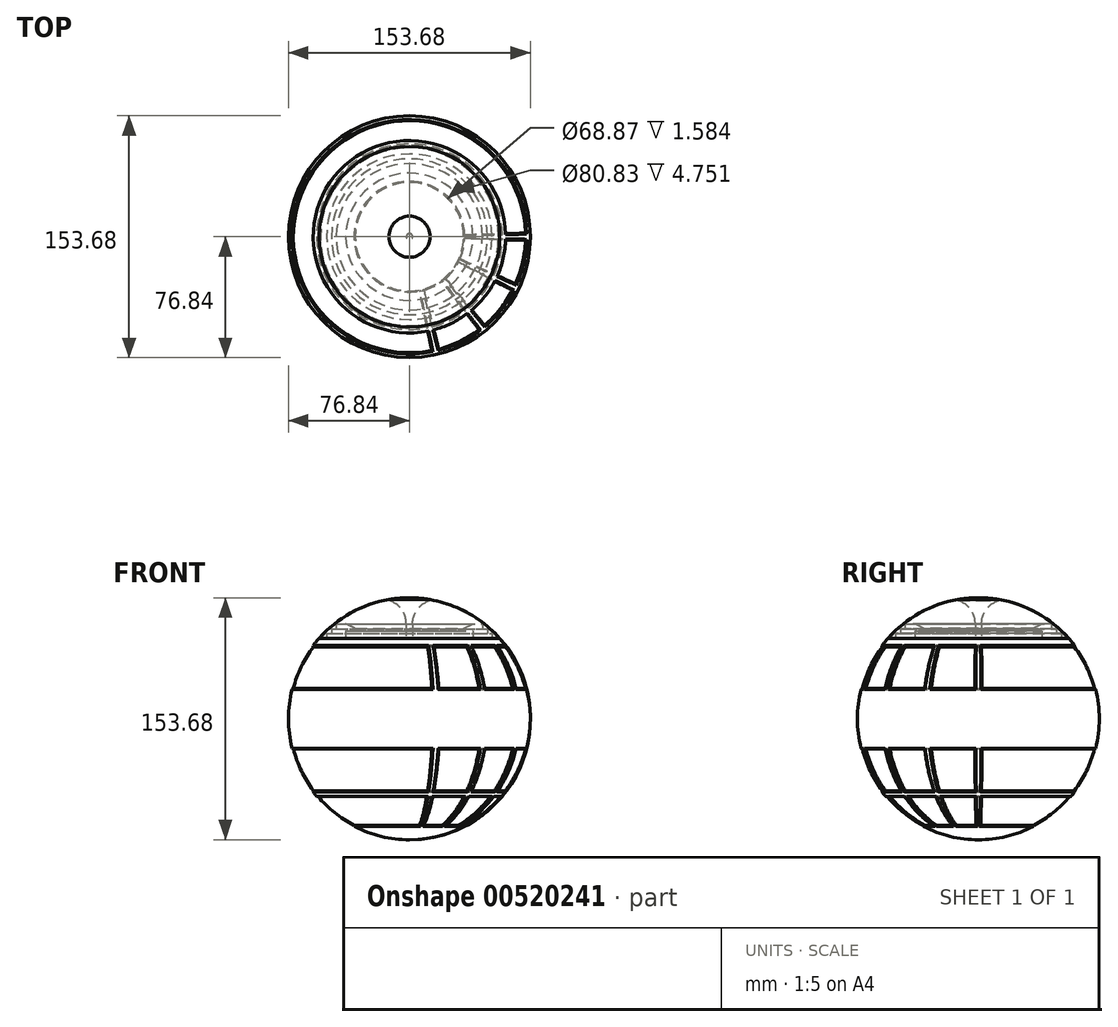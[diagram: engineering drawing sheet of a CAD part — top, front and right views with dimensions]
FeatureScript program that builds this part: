
annotation { "Feature Type Name" : "Feature", "Feature Type Description" : "" }
export const myFeature = defineFeature(function(context is Context, id is Id, definition is map)
    precondition{}
    {
        {
            var Q0;
            Q0=qCreatedBy(makeId("Front.planeOp"),FACE);
            var sketch = newSketch(context, id + "F0", { "sketchPlane" : qUnion([Q0])});
            skCircle(sketch, "E0", {"center": v(0, 0) * mm, "radius": 76.2 * mm});
            skLineSegment(sketch, "E1", {"start": v(0, 0) * mm, "end": v(74.29, 16.95) * mm, "construction": true});
            skLineSegment(sketch, "E2", {"start": v(0, 0) * mm, "end": v(74.29, -16.96) * mm, "construction": true});
            skLineSegment(sketch, "E3", {"start": v(0, 0) * mm, "end": v(59.58, -47.51) * mm, "construction": true});
            skLineSegment(sketch, "E4", {"start": v(0, 0) * mm, "end": v(33.06, -68.65) * mm, "construction": true});
            skLineSegment(sketch, "E5", {"start": v(0, 0) * mm, "end": v(0, -76.2) * mm, "construction": true});
            skLineSegment(sketch, "E6", {"start": v(0, 0) * mm, "end": v(59.58, 47.5) * mm, "construction": true});
            skLineSegment(sketch, "E7", {"start": v(0, 0) * mm, "end": v(33.06, 68.65) * mm, "construction": true});
            skLineSegment(sketch, "E8", {"start": v(0, 0) * mm, "end": v(0, 76.2) * mm, "construction": true});
            skCircle(sketch, "E9", {"center": v(0, 0) * mm, "radius": 76.83 * mm});
            skLineSegment(sketch, "E10", {"start": v(74.29, 16.95) * mm, "end": v(74.9, 17.1) * mm});
            skLineSegment(sketch, "E11", {"start": v(74.29, -16.96) * mm, "end": v(74.9, -17.1) * mm});
            skLineSegment(sketch, "E12", {"start": v(33.06, -68.65) * mm, "end": v(33.34, -69.23) * mm, "construction": true});
            skLineSegment(sketch, "E13", {"start": v(34.57, -67.9) * mm, "end": v(34.86, -68.47) * mm});
            skLineSegment(sketch, "E14", {"start": v(58.5, -48.82) * mm, "end": v(59, -49.22) * mm});
            skLineSegment(sketch, "E15", {"start": v(60.62, -46.17) * mm, "end": v(61.11, -46.57) * mm});
            skLineSegment(sketch, "E16", {"start": v(59.58, -47.51) * mm, "end": v(60.07, -47.9) * mm, "construction": true});
            skLineSegment(sketch, "E17", {"start": v(73.9, -18.6) * mm, "end": v(74.51, -18.75) * mm});
            skLineSegment(sketch, "E18", {"start": v(73.9, 18.59) * mm, "end": v(74.51, 18.74) * mm});
            skLineSegment(sketch, "E19", {"start": v(60.62, 46.17) * mm, "end": v(61.12, 46.56) * mm});
            skLineSegment(sketch, "E20", {"start": v(57.37, 51.1) * mm, "end": v(0, 51.1) * mm});
            skLineSegment(sketch, "E21", {"start": v(0, 51.1) * mm, "end": v(0, -76.84) * mm});
            skLineSegment(sketch, "E22", {"start": v(52.58, 51.1) * mm, "end": v(52.58, 54.16) * mm});
            skLineSegment(sketch, "E23", {"start": v(52.58, 54.16) * mm, "end": v(49.53, 54.16) * mm});
            skLineSegment(sketch, "E24", {"start": v(49.53, 54.16) * mm, "end": v(49.53, 57.2) * mm});
            skLineSegment(sketch, "E25", {"start": v(49.53, 57.2) * mm, "end": v(46.49, 57.2) * mm});
            skLineSegment(sketch, "E26", {"start": v(46.49, 57.2) * mm, "end": v(46.49, 60.25) * mm});
            skLineSegment(sketch, "E27", {"start": v(46.49, 60.25) * mm, "end": v(0, 60.25) * mm});
            skLineSegment(sketch, "E28", {"start": v(0, 60.25) * mm, "end": v(0, 51.1) * mm});
            skPoint(sketch, "E29", {"position": v(56.52, 51.1) * mm});
            skLineSegment(sketch, "E30", {"start": v(12.92, 75.1) * mm, "end": v(13.14, 76.35) * mm});
            skLineSegment(sketch, "E31", {"start": v(0, 76.2) * mm, "end": v(0, 77.47) * mm});
            skArc(sketch, "E32", {"start": v(0, 77.47) * mm, "mid": v(6.6, 77.19) * mm, "end": v(13.14, 76.35) * mm});
            skLineSegment(sketch, "E33", {"start": v(40.42, 60.25) * mm, "end": v(34.43, 57.44) * mm});
            skLineSegment(sketch, "E34", {"start": v(34.43, 57.44) * mm, "end": v(34.43, 55.86) * mm});
            skLineSegment(sketch, "E35", {"start": v(34.43, 55.86) * mm, "end": v(40.42, 55.86) * mm});
            skLineSegment(sketch, "E36", {"start": v(40.42, 55.86) * mm, "end": v(40.42, 51.1) * mm});
            skLineSegment(sketch, "E37", {"start": v(2, 51.1) * mm, "end": v(2, 60.25) * mm});
            skArc(sketch, "E38", {"start": v(12.92, 75.1) * mm, "mid": v(5.02, 69.47) * mm, "end": v(2, 60.25) * mm});
            skLineSegment(sketch, "E39", {"start": v(0, 76.2) * mm, "end": v(0, 60.25) * mm});
            skLineSegment(sketch, "E40", {"start": v(34.57, -67.9) * mm, "end": v(0, 0) * mm, "construction": true});
            skLineSegment(sketch, "E41", {"start": v(58.5, -48.82) * mm, "end": v(0, 0) * mm, "construction": true});
            skLineSegment(sketch, "E42", {"start": v(0, 0) * mm, "end": v(60.62, -46.17) * mm, "construction": true});
            skSolve(sketch);
        }
        {
            var Q0;
            {var subQ0=sQuery(id+"F0.wireOp",EDGE,"E0");var subQ1=makeQuery(id+"F0.imprint","INTERSECT",VERTEX,{"derivedFrom":[subQ0,sQuery(id+"F0.wireOp",EDGE,"E10")]});Q0=makeQuery(id+"F0.imprint","IMPRINT",FACE,{"disambiguationData":[TD([[makeQuery(id+"F0.imprint","IMPRINT",EDGE,{"disambiguationData":[TD([[subQ1,-1.0]])],"derivedFrom":subQ0}),1.0]])]});}
            var Q1;
            {var subQ0=sQuery(id+"F0.wireOp",EDGE,"E22");Q1=makeQuery(id+"F0.imprint","IMPRINT",FACE,{"disambiguationData":[TD([[makeQuery(id+"F0.imprint","IMPRINT",EDGE,{"derivedFrom":subQ0}),1.0]])]});}
            var Q2;
            {var subQ0=sQuery(id+"F0.wireOp",EDGE,"E19");Q2=makeQuery(id+"F0.imprint","IMPRINT",FACE,{"disambiguationData":[TD([[makeQuery(id+"F0.imprint","IMPRINT",EDGE,{"derivedFrom":subQ0}),1.0]])]});}
            var Q3;
            {var subQ0=sQuery(id+"F0.wireOp",EDGE,"E10");Q3=makeQuery(id+"F0.imprint","IMPRINT",FACE,{"disambiguationData":[TD([[makeQuery(id+"F0.imprint","IMPRINT",EDGE,{"derivedFrom":subQ0}),1.0]])]});}
            var Q4;
            {var subQ0=sQuery(id+"F0.wireOp",EDGE,"E10");Q4=makeQuery(id+"F0.imprint","IMPRINT",FACE,{"disambiguationData":[TD([[makeQuery(id+"F0.imprint","IMPRINT",EDGE,{"derivedFrom":subQ0}),-1.0]])]});}
            var Q5;
            {var subQ0=sQuery(id+"F0.wireOp",EDGE,"E11");Q5=makeQuery(id+"F0.imprint","IMPRINT",FACE,{"disambiguationData":[TD([[makeQuery(id+"F0.imprint","IMPRINT",EDGE,{"derivedFrom":subQ0}),-1.0]])]});}
            var Q6;
            {var subQ0=sQuery(id+"F0.wireOp",EDGE,"E14");Q6=makeQuery(id+"F0.imprint","IMPRINT",FACE,{"disambiguationData":[TD([[makeQuery(id+"F0.imprint","IMPRINT",EDGE,{"derivedFrom":subQ0}),1.0]])]});}
            var Q7;
            {var subQ0=sQuery(id+"F0.wireOp",EDGE,"E13");Q7=makeQuery(id+"F0.imprint","IMPRINT",FACE,{"disambiguationData":[TD([[makeQuery(id+"F0.imprint","IMPRINT",EDGE,{"derivedFrom":subQ0}),-1.0]])]});}
            var Q8;
            {var subQ0=sQuery(id+"F0.wireOp",EDGE,"E38");Q8=makeQuery(id+"F0.imprint","IMPRINT",FACE,{"disambiguationData":[TD([[makeQuery(id+"F0.imprint","IMPRINT",EDGE,{"derivedFrom":subQ0}),-1.0]])]});}
            var Q9;
            {var subQ0=sQuery(id+"F0.wireOp",EDGE,"E28");Q9=makeQuery(id+"F0.imprint","IMPRINT",FACE,{"disambiguationData":[TD([[makeQuery(id+"F0.imprint","IMPRINT",EDGE,{"derivedFrom":subQ0}),1.0]])]});}
            var Q10;
            {var subQ0=sQuery(id+"F0.wireOp",EDGE,"E30");var subQ5=sQuery(id+"F0.wireOp",EDGE,"E9");var subQ6=makeQuery(id+"F0.imprint","INTERSECT",VERTEX,{"derivedFrom":[subQ5,subQ0]});Q10=makeQuery(id+"F0.imprint","IMPRINT",FACE,{"disambiguationData":[TD([[makeQuery(id+"F0.imprint","IMPRINT",EDGE,{"disambiguationData":[TD([[subQ6,-1.0]])],"derivedFrom":subQ5}),1.0]])]});}
            var Q11;
            {var subQ5=sQuery(id+"F0.wireOp",EDGE,"E32");Q11=makeQuery(id+"F0.imprint","IMPRINT",FACE,{"disambiguationData":[TD([[makeQuery(id+"F0.imprint","IMPRINT",EDGE,{"derivedFrom":subQ5}),-1.0]])]});}
            var Q12;
            Q12=sQuery(id+"F0.wireOp",EDGE,"E8");
            revolve(context, id + "F1", {"entities" : qUnion([Q0, Q1, Q2, Q3, Q4, Q5, Q6, Q7, Q8, Q9, Q10, Q11]), "axis" : qUnion([Q12]), "revolveType" : RevolveType.FULL});
        }
        {
            var Q0;
            {var subQ3=sQuery(id+"F0.wireOp",EDGE,"E20");var subQ5=sQuery(id+"F0.wireOp",EDGE,"E9");var subQ7=makeQuery(id+"F0.imprint","INTERSECT",VERTEX,{"derivedFrom":[subQ5,subQ3]});Q0=makeQuery(id+"F0.imprint","IMPRINT",FACE,{"disambiguationData":[TD([[makeQuery(id+"F0.imprint","IMPRINT",EDGE,{"disambiguationData":[TD([[subQ7,-1.0]])],"derivedFrom":subQ5}),1.0]])]});}
            var Q1;
            Q1=sQuery(id+"F0.wireOp",EDGE,"E21");
            revolve(context, id + "F2", {"entities" : qUnion([Q0]), "axis" : qUnion([Q1]), "revolveType" : RevolveType.FULL});
        }
        {
            var Q0;
            {var subQ0=sQuery(id+"F0.wireOp",EDGE,"E18");Q0=makeQuery(id+"F0.imprint","IMPRINT",FACE,{"disambiguationData":[TD([[makeQuery(id+"F0.imprint","IMPRINT",EDGE,{"derivedFrom":subQ0}),1.0]])]});}
            var Q1;
            {var subQ0=sQuery(id+"F0.wireOp",EDGE,"E15");Q1=makeQuery(id+"F0.imprint","IMPRINT",FACE,{"disambiguationData":[TD([[makeQuery(id+"F0.imprint","IMPRINT",EDGE,{"derivedFrom":subQ0}),1.0]])]});}
            var Q2;
            {var subQ0=sQuery(id+"F0.wireOp",EDGE,"E13");Q2=makeQuery(id+"F0.imprint","IMPRINT",FACE,{"disambiguationData":[TD([[makeQuery(id+"F0.imprint","IMPRINT",EDGE,{"derivedFrom":subQ0}),1.0]])]});}
            var Q3;
            Q3=sQuery(id+"F0.wireOp",EDGE,"E21");
            revolve(context, id + "F3", {"operationType" : NewBodyOperationType.ADD, "entities" : qUnion([Q0, Q1, Q2]), "axis" : qUnion([Q3]), "revolveType" : RevolveType.SYMMETRIC, "angle" : 2.55 * degree});
        }
        {
            var Q0;
            Q0=qCreatedBy(makeId("Top.planeOp"),FACE);
            var sketch = newSketch(context, id + "F4", { "sketchPlane" : qUnion([Q0])});
            skCircle(sketch, "E43", {"center": v(0, 0) * mm, "radius": 76.83 * mm});
            skLineSegment(sketch, "E44", {"start": v(0, 0) * mm, "end": v(76.83, 0) * mm, "construction": true});
            skLineSegment(sketch, "E45", {"start": v(0, 0) * mm, "end": v(69.23, -33.34) * mm, "construction": true});
            skLineSegment(sketch, "E46", {"start": v(0, 0) * mm, "end": v(47.9, -60.07) * mm, "construction": true});
            skLineSegment(sketch, "E47", {"start": v(0, 0) * mm, "end": v(17.1, -74.9) * mm, "construction": true});
            skSolve(sketch);
        }
        {
            var Q0;
            Q0=sQuery(id+"F4.wireOp",VERTEX,"E45.end");
            var Q1;
            Q1=makeQuery(id+"F1.opRevolve","SWEPT_EDGE",EDGE,{"disambiguationData":[OSD([sQuery(id+"F0.wireOp",EDGE,"E9"),sQuery(id+"F0.wireOp",EDGE,"E18")])]});
            cPlane(context, id + "F5", {"entities" : qUnion([Q0, Q1]), "cplaneType" : CPlaneType.CURVE_POINT, "offset" : 25.4 * mm, "width" : 152.4 * mm, "height" : 152.4 * mm});
        }
        {
            var Q0;
            Q0=qCreatedBy(id+"F5.planeOp",FACE);
            var sketch = newSketch(context, id + "F6", { "sketchPlane" : qUnion([Q0])});
            skLineSegment(sketch, "E48.0", {"start": v(61.12, 46.56) * mm, "end": v(-61.12, 46.56) * mm});
            skLineSegment(sketch, "E49.0", {"start": v(34.86, -68.47) * mm, "end": v(-34.86, -68.47) * mm});
            skArc(sketch, "E50", {"start": v(61.12, 46.56) * mm, "mid": v(74.9, -17.1) * mm, "end": v(34.86, -68.47) * mm});
            skLineSegment(sketch, "E51", {"start": v(61.12, 46.56) * mm, "end": v(0, 46.56) * mm});
            skLineSegment(sketch, "E52", {"start": v(0, 46.56) * mm, "end": v(0, 0) * mm});
            skLineSegment(sketch, "E53", {"start": v(0, 0) * mm, "end": v(0, -68.47) * mm});
            skSolve(sketch);
        }
        {
            var Q0;
            Q0 = qSketchRegion(id + "F6", true);
            var Q1;
            Q1=sQuery(id+"F6.wireOp",EDGE,"E52");
            revolve(context, id + "F7", {"operationType" : NewBodyOperationType.ADD, "entities" : qUnion([Q0]), "axis" : qUnion([Q1]), "revolveType" : RevolveType.SYMMETRIC, "angle" : 2.55 * degree});
        }
        {
            var Q0;
            Q0=sQuery(id+"F4.wireOp",VERTEX,"E46.end");
            var Q1;
            Q1=sQuery(id+"F4.wireOp",EDGE,"E43");
            cPlane(context, id + "F8", {"entities" : qUnion([Q0, Q1]), "cplaneType" : CPlaneType.CURVE_POINT, "offset" : 25.4 * mm, "width" : 152.4 * mm, "height" : 152.4 * mm});
        }
        {
            var Q0;
            Q0=qCreatedBy(id+"F8.planeOp",FACE);
            var sketch = newSketch(context, id + "F9", { "sketchPlane" : qUnion([Q0])});
            skLineSegment(sketch, "E54.0", {"start": v(61.12, 46.56) * mm, "end": v(-61.12, 46.56) * mm});
            skLineSegment(sketch, "E54.1", {"start": v(34.86, -68.47) * mm, "end": v(-34.86, -68.47) * mm});
            skArc(sketch, "E55", {"start": v(-61.12, 46.56) * mm, "mid": v(-74.9, -17.1) * mm, "end": v(-34.86, -68.47) * mm});
            skLineSegment(sketch, "E56", {"start": v(-34.86, -68.47) * mm, "end": v(0, -68.47) * mm});
            skLineSegment(sketch, "E57", {"start": v(0, -68.47) * mm, "end": v(0, 0) * mm});
            skLineSegment(sketch, "E58", {"start": v(0, 0) * mm, "end": v(0, 46.56) * mm});
            skLineSegment(sketch, "E59", {"start": v(0, 46.56) * mm, "end": v(-61.12, 46.56) * mm});
            skSolve(sketch);
        }
        {
            var Q0;
            Q0 = qSketchRegion(id + "F9", true);
            var Q1;
            Q1=sQuery(id+"F9.wireOp",EDGE,"E58");
            revolve(context, id + "F10", {"operationType" : NewBodyOperationType.ADD, "entities" : qUnion([Q0]), "axis" : qUnion([Q1]), "revolveType" : RevolveType.SYMMETRIC, "angle" : 2.55 * degree});
        }
        {
            var Q0;
            Q0=sQuery(id+"F4.wireOp",EDGE,"E43");
            var Q1;
            Q1=sQuery(id+"F4.wireOp",VERTEX,"E47.end");
            cPlane(context, id + "F11", {"entities" : qUnion([Q0, Q1]), "cplaneType" : CPlaneType.CURVE_POINT, "offset" : 25.4 * mm, "width" : 152.4 * mm, "height" : 152.4 * mm});
        }
        {
            var Q0;
            Q0=qCreatedBy(id+"F11.planeOp",FACE);
            var sketch = newSketch(context, id + "F12", { "sketchPlane" : qUnion([Q0])});
            skLineSegment(sketch, "E60.0", {"start": v(34.86, -68.47) * mm, "end": v(-34.86, -68.47) * mm});
            skLineSegment(sketch, "E60.1", {"start": v(61.12, 46.56) * mm, "end": v(-61.12, 46.56) * mm});
            skLineSegment(sketch, "E61", {"start": v(0, 0) * mm, "end": v(0, 46.56) * mm});
            skLineSegment(sketch, "E62", {"start": v(0, 0) * mm, "end": v(0, -68.47) * mm});
            skArc(sketch, "E63", {"start": v(-61.12, 46.56) * mm, "mid": v(-74.9, -17.1) * mm, "end": v(-34.86, -68.47) * mm});
            skSolve(sketch);
        }
        {
            var Q0;
            Q0 = qSketchRegion(id + "F12", true);
            var Q1;
            Q1=sQuery(id+"F12.wireOp",EDGE,"E61");
            revolve(context, id + "F13", {"operationType" : NewBodyOperationType.ADD, "entities" : qUnion([Q0]), "axis" : qUnion([Q1]), "revolveType" : RevolveType.SYMMETRIC, "angle" : 2.55 * degree});
        }
        {
            var Q0;
            {var subQ0=sQuery(id+"F0.wireOp",EDGE,"E18");var subQ2=sQuery(id+"F0.wireOp",EDGE,"E19");var subQ4=makeQuery(id+"F10.opRevolve","CAP_FACE",FACE,{"disambiguationData":[OSD([sQuery(id+"F9.wireOp",EDGE,"E55"),sQuery(id+"F9.wireOp",EDGE,"E56"),sQuery(id+"F9.wireOp",EDGE,"E57"),sQuery(id+"F9.wireOp",EDGE,"E58"),sQuery(id+"F9.wireOp",EDGE,"E59")])],"isStart":true});var subQ5=sQuery(id+"F0.wireOp",EDGE,"E0");var subQ6=makeQuery(id+"F3.opRevolve","CAP_FACE",FACE,{"disambiguationData":[OSD([subQ5,sQuery(id+"F0.wireOp",EDGE,"E9"),subQ0,subQ2])],"isStart":true});Q0=makeQuery(id+"F13.boolean.opBoolean","SPLIT",FACE,{"disambiguationData":[TD([subQ4])],"derivedFrom":makeQuery(id+"F10.boolean.opBoolean","SPLIT",FACE,{"disambiguationData":[TD([subQ6])],"derivedFrom":makeQuery(id+"F7.boolean.opBoolean","SPLIT",FACE,{"disambiguationData":[TD([subQ6])],"derivedFrom":makeQuery(id+"F1.opRevolve","SWEPT_FACE",FACE,{"disambiguationData":[OSD([subQ5]),TDD([makeQuery(id+"F0.imprint","IMPRINT",EDGE,{"disambiguationData":[TD([[makeQuery(id+"F0.imprint","INTERSECT",VERTEX,{"derivedFrom":[subQ5,subQ0]}),-1.0]])],"derivedFrom":subQ5})])]})})})});}
            var Q1;
            {var subQ0=sQuery(id+"F0.wireOp",EDGE,"E18");var subQ2=makeQuery(id+"F7.opRevolve","CAP_FACE",FACE,{"disambiguationData":[OSD([sQuery(id+"F6.wireOp",EDGE,"E49.0"),sQuery(id+"F6.wireOp",EDGE,"E50"),sQuery(id+"F6.wireOp",EDGE,"E51"),sQuery(id+"F6.wireOp",EDGE,"E52"),sQuery(id+"F6.wireOp",EDGE,"E53")])],"isStart":false});var subQ3=sQuery(id+"F0.wireOp",EDGE,"E19");var subQ5=sQuery(id+"F0.wireOp",EDGE,"E0");Q1=makeQuery(id+"F10.boolean.opBoolean","SPLIT",FACE,{"disambiguationData":[TD([subQ2])],"derivedFrom":makeQuery(id+"F7.boolean.opBoolean","SPLIT",FACE,{"disambiguationData":[TD([makeQuery(id+"F3.opRevolve","CAP_FACE",FACE,{"disambiguationData":[OSD([subQ5,sQuery(id+"F0.wireOp",EDGE,"E9"),subQ0,subQ3])],"isStart":true})])],"derivedFrom":makeQuery(id+"F1.opRevolve","SWEPT_FACE",FACE,{"disambiguationData":[OSD([subQ5]),TDD([makeQuery(id+"F0.imprint","IMPRINT",EDGE,{"disambiguationData":[TD([[makeQuery(id+"F0.imprint","INTERSECT",VERTEX,{"derivedFrom":[subQ5,subQ0]}),-1.0]])],"derivedFrom":subQ5})])]})})});}
            var Q2;
            {var subQ0=sQuery(id+"F0.wireOp",EDGE,"E18");var subQ1=sQuery(id+"F0.wireOp",EDGE,"E19");var subQ2=sQuery(id+"F0.wireOp",EDGE,"E0");Q2=makeQuery(id+"F7.boolean.opBoolean","SPLIT",FACE,{"disambiguationData":[TD([makeQuery(id+"F3.opRevolve","CAP_FACE",FACE,{"disambiguationData":[OSD([subQ2,sQuery(id+"F0.wireOp",EDGE,"E9"),subQ0,subQ1])],"isStart":false})])],"derivedFrom":makeQuery(id+"F1.opRevolve","SWEPT_FACE",FACE,{"disambiguationData":[OSD([subQ2]),TDD([makeQuery(id+"F0.imprint","IMPRINT",EDGE,{"disambiguationData":[TD([[makeQuery(id+"F0.imprint","INTERSECT",VERTEX,{"derivedFrom":[subQ2,subQ0]}),-1.0]])],"derivedFrom":subQ2})])]})});}
            var Q3;
            {var subQ0=sQuery(id+"F0.wireOp",EDGE,"E15");var subQ1=sQuery(id+"F0.wireOp",EDGE,"E17");var subQ2=sQuery(id+"F0.wireOp",EDGE,"E0");Q3=makeQuery(id+"F7.boolean.opBoolean","SPLIT",FACE,{"disambiguationData":[TD([makeQuery(id+"F3.opRevolve","CAP_FACE",FACE,{"disambiguationData":[OSD([subQ2,sQuery(id+"F0.wireOp",EDGE,"E9"),subQ0,subQ1])],"isStart":false})])],"derivedFrom":makeQuery(id+"F1.opRevolve","SWEPT_FACE",FACE,{"disambiguationData":[OSD([subQ2]),TDD([makeQuery(id+"F0.imprint","IMPRINT",EDGE,{"disambiguationData":[TD([[makeQuery(id+"F0.imprint","INTERSECT",VERTEX,{"derivedFrom":[subQ2,subQ0]}),-1.0]])],"derivedFrom":subQ2})])]})});}
            var Q4;
            {var subQ0=sQuery(id+"F0.wireOp",EDGE,"E15");var subQ2=sQuery(id+"F0.wireOp",EDGE,"E17");var subQ4=makeQuery(id+"F7.opRevolve","CAP_FACE",FACE,{"disambiguationData":[OSD([sQuery(id+"F6.wireOp",EDGE,"E49.0"),sQuery(id+"F6.wireOp",EDGE,"E50"),sQuery(id+"F6.wireOp",EDGE,"E51"),sQuery(id+"F6.wireOp",EDGE,"E52"),sQuery(id+"F6.wireOp",EDGE,"E53")])],"isStart":false});var subQ5=sQuery(id+"F0.wireOp",EDGE,"E0");Q4=makeQuery(id+"F10.boolean.opBoolean","SPLIT",FACE,{"disambiguationData":[TD([subQ4])],"derivedFrom":makeQuery(id+"F7.boolean.opBoolean","SPLIT",FACE,{"disambiguationData":[TD([makeQuery(id+"F3.opRevolve","CAP_FACE",FACE,{"disambiguationData":[OSD([subQ5,sQuery(id+"F0.wireOp",EDGE,"E9"),subQ0,subQ2])],"isStart":true})])],"derivedFrom":makeQuery(id+"F1.opRevolve","SWEPT_FACE",FACE,{"disambiguationData":[OSD([subQ5]),TDD([makeQuery(id+"F0.imprint","IMPRINT",EDGE,{"disambiguationData":[TD([[makeQuery(id+"F0.imprint","INTERSECT",VERTEX,{"derivedFrom":[subQ5,subQ0]}),-1.0]])],"derivedFrom":subQ5})])]})})});}
            var Q5;
            {var subQ0=sQuery(id+"F0.wireOp",EDGE,"E15");var subQ2=sQuery(id+"F0.wireOp",EDGE,"E17");var subQ4=makeQuery(id+"F10.opRevolve","CAP_FACE",FACE,{"disambiguationData":[OSD([sQuery(id+"F9.wireOp",EDGE,"E55"),sQuery(id+"F9.wireOp",EDGE,"E56"),sQuery(id+"F9.wireOp",EDGE,"E57"),sQuery(id+"F9.wireOp",EDGE,"E58"),sQuery(id+"F9.wireOp",EDGE,"E59")])],"isStart":true});var subQ5=sQuery(id+"F0.wireOp",EDGE,"E0");var subQ6=makeQuery(id+"F3.opRevolve","CAP_FACE",FACE,{"disambiguationData":[OSD([subQ5,sQuery(id+"F0.wireOp",EDGE,"E9"),subQ0,subQ2])],"isStart":true});Q5=makeQuery(id+"F13.boolean.opBoolean","SPLIT",FACE,{"disambiguationData":[TD([subQ4])],"derivedFrom":makeQuery(id+"F10.boolean.opBoolean","SPLIT",FACE,{"disambiguationData":[TD([subQ6])],"derivedFrom":makeQuery(id+"F7.boolean.opBoolean","SPLIT",FACE,{"disambiguationData":[TD([subQ6])],"derivedFrom":makeQuery(id+"F1.opRevolve","SWEPT_FACE",FACE,{"disambiguationData":[OSD([subQ5]),TDD([makeQuery(id+"F0.imprint","IMPRINT",EDGE,{"disambiguationData":[TD([[makeQuery(id+"F0.imprint","INTERSECT",VERTEX,{"derivedFrom":[subQ5,subQ0]}),-1.0]])],"derivedFrom":subQ5})])]})})})});}
            var Q6;
            {var subQ0=sQuery(id+"F0.wireOp",EDGE,"E13");var subQ2=sQuery(id+"F0.wireOp",EDGE,"E14");var subQ4=makeQuery(id+"F10.opRevolve","CAP_FACE",FACE,{"disambiguationData":[OSD([sQuery(id+"F9.wireOp",EDGE,"E55"),sQuery(id+"F9.wireOp",EDGE,"E56"),sQuery(id+"F9.wireOp",EDGE,"E57"),sQuery(id+"F9.wireOp",EDGE,"E58"),sQuery(id+"F9.wireOp",EDGE,"E59")])],"isStart":true});var subQ5=sQuery(id+"F0.wireOp",EDGE,"E0");var subQ6=makeQuery(id+"F3.opRevolve","CAP_FACE",FACE,{"disambiguationData":[OSD([subQ5,sQuery(id+"F0.wireOp",EDGE,"E9"),subQ0,subQ2])],"isStart":true});Q6=makeQuery(id+"F13.boolean.opBoolean","SPLIT",FACE,{"disambiguationData":[TD([subQ4])],"derivedFrom":makeQuery(id+"F10.boolean.opBoolean","SPLIT",FACE,{"disambiguationData":[TD([subQ6])],"derivedFrom":makeQuery(id+"F7.boolean.opBoolean","SPLIT",FACE,{"disambiguationData":[TD([subQ6])],"derivedFrom":makeQuery(id+"F1.opRevolve","SWEPT_FACE",FACE,{"disambiguationData":[OSD([subQ5]),TDD([makeQuery(id+"F0.imprint","IMPRINT",EDGE,{"disambiguationData":[TD([[makeQuery(id+"F0.imprint","INTERSECT",VERTEX,{"derivedFrom":[subQ5,subQ0]}),-1.0]])],"derivedFrom":subQ5})])]})})})});}
            var Q7;
            {var subQ0=sQuery(id+"F0.wireOp",EDGE,"E13");var subQ2=sQuery(id+"F0.wireOp",EDGE,"E14");var subQ4=makeQuery(id+"F7.opRevolve","CAP_FACE",FACE,{"disambiguationData":[OSD([sQuery(id+"F6.wireOp",EDGE,"E49.0"),sQuery(id+"F6.wireOp",EDGE,"E50"),sQuery(id+"F6.wireOp",EDGE,"E51"),sQuery(id+"F6.wireOp",EDGE,"E52"),sQuery(id+"F6.wireOp",EDGE,"E53")])],"isStart":false});var subQ5=sQuery(id+"F0.wireOp",EDGE,"E0");Q7=makeQuery(id+"F10.boolean.opBoolean","SPLIT",FACE,{"disambiguationData":[TD([subQ4])],"derivedFrom":makeQuery(id+"F7.boolean.opBoolean","SPLIT",FACE,{"disambiguationData":[TD([makeQuery(id+"F3.opRevolve","CAP_FACE",FACE,{"disambiguationData":[OSD([subQ5,sQuery(id+"F0.wireOp",EDGE,"E9"),subQ0,subQ2])],"isStart":true})])],"derivedFrom":makeQuery(id+"F1.opRevolve","SWEPT_FACE",FACE,{"disambiguationData":[OSD([subQ5]),TDD([makeQuery(id+"F0.imprint","IMPRINT",EDGE,{"disambiguationData":[TD([[makeQuery(id+"F0.imprint","INTERSECT",VERTEX,{"derivedFrom":[subQ5,subQ0]}),-1.0]])],"derivedFrom":subQ5})])]})})});}
            var Q8;
            {var subQ0=sQuery(id+"F0.wireOp",EDGE,"E13");var subQ1=sQuery(id+"F0.wireOp",EDGE,"E14");var subQ2=sQuery(id+"F0.wireOp",EDGE,"E0");Q8=makeQuery(id+"F7.boolean.opBoolean","SPLIT",FACE,{"disambiguationData":[TD([makeQuery(id+"F3.opRevolve","CAP_FACE",FACE,{"disambiguationData":[OSD([subQ2,sQuery(id+"F0.wireOp",EDGE,"E9"),subQ0,subQ1])],"isStart":false})])],"derivedFrom":makeQuery(id+"F1.opRevolve","SWEPT_FACE",FACE,{"disambiguationData":[OSD([subQ2]),TDD([makeQuery(id+"F0.imprint","IMPRINT",EDGE,{"disambiguationData":[TD([[makeQuery(id+"F0.imprint","INTERSECT",VERTEX,{"derivedFrom":[subQ2,subQ0]}),-1.0]])],"derivedFrom":subQ2})])]})});}
            var Q9;
            {var subQ0=sQuery(id+"F0.wireOp",EDGE,"E18");var subQ2=sQuery(id+"F0.wireOp",EDGE,"E19");var subQ9=sQuery(id+"F0.wireOp",EDGE,"E0");var subQ10=makeQuery(id+"F3.opRevolve","CAP_FACE",FACE,{"disambiguationData":[OSD([subQ9,sQuery(id+"F0.wireOp",EDGE,"E9"),subQ0,subQ2])],"isStart":true});Q9=makeQuery(id+"FeTh8RoejFn6YHX_2.1.F7.boolean.opBoolean","SPLIT",FACE,{"disambiguationData":[TD([subQ10])],"derivedFrom":makeQuery(id+"F13.boolean.opBoolean","SPLIT",FACE,{"disambiguationData":[TD([subQ10])],"derivedFrom":makeQuery(id+"F10.boolean.opBoolean","SPLIT",FACE,{"disambiguationData":[TD([subQ10])],"derivedFrom":makeQuery(id+"F7.boolean.opBoolean","SPLIT",FACE,{"disambiguationData":[TD([subQ10])],"derivedFrom":makeQuery(id+"F1.opRevolve","SWEPT_FACE",FACE,{"disambiguationData":[OSD([subQ9]),TDD([makeQuery(id+"F0.imprint","IMPRINT",EDGE,{"disambiguationData":[TD([[makeQuery(id+"F0.imprint","INTERSECT",VERTEX,{"derivedFrom":[subQ9,subQ0]}),-1.0]])],"derivedFrom":subQ9})])]})})})})});}
            var Q10;
            {var subQ0=sQuery(id+"F0.wireOp",EDGE,"E18");var subQ7=sQuery(id+"F0.wireOp",EDGE,"E19");var subQ9=sQuery(id+"F6.wireOp",EDGE,"E53");var subQ10=sQuery(id+"F6.wireOp",EDGE,"E52");var subQ11=sQuery(id+"F6.wireOp",EDGE,"E51");var subQ12=sQuery(id+"F6.wireOp",EDGE,"E50");var subQ13=sQuery(id+"F6.wireOp",EDGE,"E49.0");var subQ14=makeQuery(id+"FeTh8RoejFn6YHX_2.1.F7.opRevolve","CAP_FACE",FACE,{"disambiguationData":[OSD([subQ13,subQ12,subQ11,subQ10,subQ9])],"isStart":false});var subQ15=makeQuery(id+"F13.opRevolve","CAP_FACE",FACE,{"disambiguationData":[OSD([sQuery(id+"F12.wireOp",EDGE,"E60.0"),sQuery(id+"F12.wireOp",EDGE,"E60.1"),sQuery(id+"F12.wireOp",EDGE,"E61"),sQuery(id+"F12.wireOp",EDGE,"E62"),sQuery(id+"F12.wireOp",EDGE,"E63")])],"isStart":true});var subQ16=sQuery(id+"F0.wireOp",EDGE,"E0");var subQ17=makeQuery(id+"F3.opRevolve","CAP_FACE",FACE,{"disambiguationData":[OSD([subQ16,sQuery(id+"F0.wireOp",EDGE,"E9"),subQ0,subQ7])],"isStart":true});Q10=makeQuery(id+"FeTh8RoejFn6YHX_2.1.F10.boolean.opBoolean","SPLIT",FACE,{"disambiguationData":[TD([subQ14])],"derivedFrom":makeQuery(id+"FeTh8RoejFn6YHX_2.1.F7.boolean.opBoolean","SPLIT",FACE,{"disambiguationData":[TD([subQ15])],"derivedFrom":makeQuery(id+"F13.boolean.opBoolean","SPLIT",FACE,{"disambiguationData":[TD([subQ17])],"derivedFrom":makeQuery(id+"F10.boolean.opBoolean","SPLIT",FACE,{"disambiguationData":[TD([subQ17])],"derivedFrom":makeQuery(id+"F7.boolean.opBoolean","SPLIT",FACE,{"disambiguationData":[TD([subQ17])],"derivedFrom":makeQuery(id+"F1.opRevolve","SWEPT_FACE",FACE,{"disambiguationData":[OSD([subQ16]),TDD([makeQuery(id+"F0.imprint","IMPRINT",EDGE,{"disambiguationData":[TD([[makeQuery(id+"F0.imprint","INTERSECT",VERTEX,{"derivedFrom":[subQ16,subQ0]}),-1.0]])],"derivedFrom":subQ16})])]})})})})})});}
            var Q11;
            {var subQ0=sQuery(id+"F0.wireOp",EDGE,"E18");var subQ2=sQuery(id+"F0.wireOp",EDGE,"E19");var subQ4=sQuery(id+"F9.wireOp",EDGE,"E59");var subQ5=sQuery(id+"F9.wireOp",EDGE,"E58");var subQ6=sQuery(id+"F9.wireOp",EDGE,"E57");var subQ7=sQuery(id+"F9.wireOp",EDGE,"E56");var subQ8=sQuery(id+"F9.wireOp",EDGE,"E55");var subQ9=makeQuery(id+"FeTh8RoejFn6YHX_2.1.F10.opRevolve","CAP_FACE",FACE,{"disambiguationData":[OSD([subQ8,subQ7,subQ6,subQ5,subQ4])],"isStart":true});var subQ10=sQuery(id+"F12.wireOp",EDGE,"E63");var subQ11=sQuery(id+"F12.wireOp",EDGE,"E62");var subQ12=sQuery(id+"F12.wireOp",EDGE,"E61");var subQ13=sQuery(id+"F12.wireOp",EDGE,"E60.1");var subQ14=sQuery(id+"F12.wireOp",EDGE,"E60.0");var subQ15=makeQuery(id+"F13.opRevolve","CAP_FACE",FACE,{"disambiguationData":[OSD([subQ14,subQ13,subQ12,subQ11,subQ10])],"isStart":true});var subQ21=sQuery(id+"F0.wireOp",EDGE,"E0");var subQ22=makeQuery(id+"F3.opRevolve","CAP_FACE",FACE,{"disambiguationData":[OSD([subQ21,sQuery(id+"F0.wireOp",EDGE,"E9"),subQ0,subQ2])],"isStart":true});Q11=makeQuery(id+"FeTh8RoejFn6YHX_2.1.F13.boolean.opBoolean","SPLIT",FACE,{"disambiguationData":[TD([subQ9])],"derivedFrom":makeQuery(id+"FeTh8RoejFn6YHX_2.1.F10.boolean.opBoolean","SPLIT",FACE,{"disambiguationData":[TD([subQ15])],"derivedFrom":makeQuery(id+"FeTh8RoejFn6YHX_2.1.F7.boolean.opBoolean","SPLIT",FACE,{"disambiguationData":[TD([subQ15])],"derivedFrom":makeQuery(id+"F13.boolean.opBoolean","SPLIT",FACE,{"disambiguationData":[TD([subQ22])],"derivedFrom":makeQuery(id+"F10.boolean.opBoolean","SPLIT",FACE,{"disambiguationData":[TD([subQ22])],"derivedFrom":makeQuery(id+"F7.boolean.opBoolean","SPLIT",FACE,{"disambiguationData":[TD([subQ22])],"derivedFrom":makeQuery(id+"F1.opRevolve","SWEPT_FACE",FACE,{"disambiguationData":[OSD([subQ21]),TDD([makeQuery(id+"F0.imprint","IMPRINT",EDGE,{"disambiguationData":[TD([[makeQuery(id+"F0.imprint","INTERSECT",VERTEX,{"derivedFrom":[subQ21,subQ0]}),-1.0]])],"derivedFrom":subQ21})])]})})})})})})});}
            var Q12;
            {var subQ0=sQuery(id+"F0.wireOp",EDGE,"E18");var subQ2=sQuery(id+"F0.wireOp",EDGE,"E19");var subQ4=sQuery(id+"F12.wireOp",EDGE,"E63");var subQ5=sQuery(id+"F12.wireOp",EDGE,"E62");var subQ6=sQuery(id+"F12.wireOp",EDGE,"E61");var subQ7=sQuery(id+"F12.wireOp",EDGE,"E60.1");var subQ8=sQuery(id+"F12.wireOp",EDGE,"E60.0");var subQ9=makeQuery(id+"FeTh8RoejFn6YHX_2.1.F13.opRevolve","CAP_FACE",FACE,{"disambiguationData":[OSD([subQ8,subQ7,subQ6,subQ5,subQ4])],"isStart":true});var subQ20=sQuery(id+"F0.wireOp",EDGE,"E9");var subQ21=sQuery(id+"F0.wireOp",EDGE,"E0");var subQ22=makeQuery(id+"F13.opRevolve","CAP_FACE",FACE,{"disambiguationData":[OSD([subQ8,subQ7,subQ6,subQ5,subQ4])],"isStart":true});var subQ23=makeQuery(id+"F3.opRevolve","CAP_FACE",FACE,{"disambiguationData":[OSD([subQ21,subQ20,subQ0,subQ2])],"isStart":true});Q12=makeQuery(id+"FgpSSfUhpf4qGKz_2.1.FeTh8RoejFn6YHX_2.1.F13.boolean.opBoolean","SPLIT",FACE,{"disambiguationData":[TD([subQ9])],"derivedFrom":makeQuery(id+"FgpSSfUhpf4qGKz_2.1.FeTh8RoejFn6YHX_2.1.F10.boolean.opBoolean","SPLIT",FACE,{"disambiguationData":[TD([subQ9])],"derivedFrom":makeQuery(id+"FgpSSfUhpf4qGKz_2.1.FeTh8RoejFn6YHX_2.1.F7.boolean.opBoolean","SPLIT",FACE,{"disambiguationData":[TD([subQ9])],"derivedFrom":makeQuery(id+"FgpSSfUhpf4qGKz_2.1.F3.boolean.opBoolean","SPLIT",FACE,{"disambiguationData":[TD([makeQuery(id+"FgpSSfUhpf4qGKz_2.1.F3.opRevolve","CAP_FACE",FACE,{"disambiguationData":[OSD([subQ21,subQ20,subQ0,subQ2])],"isStart":true})])],"derivedFrom":makeQuery(id+"FeTh8RoejFn6YHX_2.1.F13.boolean.opBoolean","SPLIT",FACE,{"disambiguationData":[TD([subQ22])],"derivedFrom":makeQuery(id+"FeTh8RoejFn6YHX_2.1.F10.boolean.opBoolean","SPLIT",FACE,{"disambiguationData":[TD([subQ22])],"derivedFrom":makeQuery(id+"FeTh8RoejFn6YHX_2.1.F7.boolean.opBoolean","SPLIT",FACE,{"disambiguationData":[TD([subQ22])],"derivedFrom":makeQuery(id+"F13.boolean.opBoolean","SPLIT",FACE,{"disambiguationData":[TD([subQ23])],"derivedFrom":makeQuery(id+"F10.boolean.opBoolean","SPLIT",FACE,{"disambiguationData":[TD([subQ23])],"derivedFrom":makeQuery(id+"F7.boolean.opBoolean","SPLIT",FACE,{"disambiguationData":[TD([subQ23])],"derivedFrom":makeQuery(id+"F1.opRevolve","SWEPT_FACE",FACE,{"disambiguationData":[OSD([subQ21]),TDD([makeQuery(id+"F0.imprint","IMPRINT",EDGE,{"disambiguationData":[TD([[makeQuery(id+"F0.imprint","INTERSECT",VERTEX,{"derivedFrom":[subQ21,subQ0]}),-1.0]])],"derivedFrom":subQ21})])]})})})})})})})})})})});}
            var Q13;
            {var subQ0=sQuery(id+"F0.wireOp",EDGE,"E18");var subQ2=sQuery(id+"F9.wireOp",EDGE,"E59");var subQ3=sQuery(id+"F9.wireOp",EDGE,"E58");var subQ4=sQuery(id+"F9.wireOp",EDGE,"E57");var subQ5=sQuery(id+"F9.wireOp",EDGE,"E56");var subQ6=sQuery(id+"F9.wireOp",EDGE,"E55");var subQ7=makeQuery(id+"FgpSSfUhpf4qGKz_2.1.FeTh8RoejFn6YHX_2.1.F10.opRevolve","CAP_FACE",FACE,{"disambiguationData":[OSD([subQ6,subQ5,subQ4,subQ3,subQ2])],"isStart":true});var subQ8=sQuery(id+"F0.wireOp",EDGE,"E19");var subQ10=sQuery(id+"F12.wireOp",EDGE,"E63");var subQ11=sQuery(id+"F12.wireOp",EDGE,"E62");var subQ12=sQuery(id+"F12.wireOp",EDGE,"E61");var subQ13=sQuery(id+"F12.wireOp",EDGE,"E60.1");var subQ14=sQuery(id+"F12.wireOp",EDGE,"E60.0");var subQ15=makeQuery(id+"FeTh8RoejFn6YHX_2.1.F13.opRevolve","CAP_FACE",FACE,{"disambiguationData":[OSD([subQ14,subQ13,subQ12,subQ11,subQ10])],"isStart":true});var subQ21=sQuery(id+"F0.wireOp",EDGE,"E9");var subQ22=sQuery(id+"F0.wireOp",EDGE,"E0");var subQ23=makeQuery(id+"F13.opRevolve","CAP_FACE",FACE,{"disambiguationData":[OSD([subQ14,subQ13,subQ12,subQ11,subQ10])],"isStart":true});var subQ24=makeQuery(id+"F3.opRevolve","CAP_FACE",FACE,{"disambiguationData":[OSD([subQ22,subQ21,subQ0,subQ8])],"isStart":true});Q13=makeQuery(id+"FgpSSfUhpf4qGKz_2.1.FeTh8RoejFn6YHX_2.1.F13.boolean.opBoolean","SPLIT",FACE,{"disambiguationData":[TD([subQ7])],"derivedFrom":makeQuery(id+"FgpSSfUhpf4qGKz_2.1.FeTh8RoejFn6YHX_2.1.F10.boolean.opBoolean","SPLIT",FACE,{"disambiguationData":[TD([subQ15])],"derivedFrom":makeQuery(id+"FgpSSfUhpf4qGKz_2.1.FeTh8RoejFn6YHX_2.1.F7.boolean.opBoolean","SPLIT",FACE,{"disambiguationData":[TD([subQ15])],"derivedFrom":makeQuery(id+"FgpSSfUhpf4qGKz_2.1.F3.boolean.opBoolean","SPLIT",FACE,{"disambiguationData":[TD([makeQuery(id+"FgpSSfUhpf4qGKz_2.1.F3.opRevolve","CAP_FACE",FACE,{"disambiguationData":[OSD([subQ22,subQ21,subQ0,subQ8])],"isStart":true})])],"derivedFrom":makeQuery(id+"FeTh8RoejFn6YHX_2.1.F13.boolean.opBoolean","SPLIT",FACE,{"disambiguationData":[TD([subQ23])],"derivedFrom":makeQuery(id+"FeTh8RoejFn6YHX_2.1.F10.boolean.opBoolean","SPLIT",FACE,{"disambiguationData":[TD([subQ23])],"derivedFrom":makeQuery(id+"FeTh8RoejFn6YHX_2.1.F7.boolean.opBoolean","SPLIT",FACE,{"disambiguationData":[TD([subQ23])],"derivedFrom":makeQuery(id+"F13.boolean.opBoolean","SPLIT",FACE,{"disambiguationData":[TD([subQ24])],"derivedFrom":makeQuery(id+"F10.boolean.opBoolean","SPLIT",FACE,{"disambiguationData":[TD([subQ24])],"derivedFrom":makeQuery(id+"F7.boolean.opBoolean","SPLIT",FACE,{"disambiguationData":[TD([subQ24])],"derivedFrom":makeQuery(id+"F1.opRevolve","SWEPT_FACE",FACE,{"disambiguationData":[OSD([subQ22]),TDD([makeQuery(id+"F0.imprint","IMPRINT",EDGE,{"disambiguationData":[TD([[makeQuery(id+"F0.imprint","INTERSECT",VERTEX,{"derivedFrom":[subQ22,subQ0]}),-1.0]])],"derivedFrom":subQ22})])]})})})})})})})})})})});}
            var Q14;
            {var subQ0=sQuery(id+"F0.wireOp",EDGE,"E18");var subQ2=sQuery(id+"F0.wireOp",EDGE,"E19");var subQ9=sQuery(id+"F6.wireOp",EDGE,"E53");var subQ10=sQuery(id+"F6.wireOp",EDGE,"E52");var subQ11=sQuery(id+"F6.wireOp",EDGE,"E51");var subQ12=sQuery(id+"F6.wireOp",EDGE,"E50");var subQ13=sQuery(id+"F6.wireOp",EDGE,"E49.0");var subQ14=makeQuery(id+"FgpSSfUhpf4qGKz_2.1.FeTh8RoejFn6YHX_2.1.F7.opRevolve","CAP_FACE",FACE,{"disambiguationData":[OSD([subQ13,subQ12,subQ11,subQ10,subQ9])],"isStart":false});var subQ15=sQuery(id+"F12.wireOp",EDGE,"E63");var subQ16=sQuery(id+"F12.wireOp",EDGE,"E62");var subQ17=sQuery(id+"F12.wireOp",EDGE,"E61");var subQ18=sQuery(id+"F12.wireOp",EDGE,"E60.1");var subQ19=sQuery(id+"F12.wireOp",EDGE,"E60.0");var subQ20=makeQuery(id+"FeTh8RoejFn6YHX_2.1.F13.opRevolve","CAP_FACE",FACE,{"disambiguationData":[OSD([subQ19,subQ18,subQ17,subQ16,subQ15])],"isStart":true});var subQ21=sQuery(id+"F0.wireOp",EDGE,"E9");var subQ22=sQuery(id+"F0.wireOp",EDGE,"E0");var subQ23=makeQuery(id+"F13.opRevolve","CAP_FACE",FACE,{"disambiguationData":[OSD([subQ19,subQ18,subQ17,subQ16,subQ15])],"isStart":true});var subQ24=makeQuery(id+"F3.opRevolve","CAP_FACE",FACE,{"disambiguationData":[OSD([subQ22,subQ21,subQ0,subQ2])],"isStart":true});Q14=makeQuery(id+"FgpSSfUhpf4qGKz_2.1.FeTh8RoejFn6YHX_2.1.F10.boolean.opBoolean","SPLIT",FACE,{"disambiguationData":[TD([subQ14])],"derivedFrom":makeQuery(id+"FgpSSfUhpf4qGKz_2.1.FeTh8RoejFn6YHX_2.1.F7.boolean.opBoolean","SPLIT",FACE,{"disambiguationData":[TD([subQ20])],"derivedFrom":makeQuery(id+"FgpSSfUhpf4qGKz_2.1.F3.boolean.opBoolean","SPLIT",FACE,{"disambiguationData":[TD([makeQuery(id+"FgpSSfUhpf4qGKz_2.1.F3.opRevolve","CAP_FACE",FACE,{"disambiguationData":[OSD([subQ22,subQ21,subQ0,subQ2])],"isStart":true})])],"derivedFrom":makeQuery(id+"FeTh8RoejFn6YHX_2.1.F13.boolean.opBoolean","SPLIT",FACE,{"disambiguationData":[TD([subQ23])],"derivedFrom":makeQuery(id+"FeTh8RoejFn6YHX_2.1.F10.boolean.opBoolean","SPLIT",FACE,{"disambiguationData":[TD([subQ23])],"derivedFrom":makeQuery(id+"FeTh8RoejFn6YHX_2.1.F7.boolean.opBoolean","SPLIT",FACE,{"disambiguationData":[TD([subQ23])],"derivedFrom":makeQuery(id+"F13.boolean.opBoolean","SPLIT",FACE,{"disambiguationData":[TD([subQ24])],"derivedFrom":makeQuery(id+"F10.boolean.opBoolean","SPLIT",FACE,{"disambiguationData":[TD([subQ24])],"derivedFrom":makeQuery(id+"F7.boolean.opBoolean","SPLIT",FACE,{"disambiguationData":[TD([subQ24])],"derivedFrom":makeQuery(id+"F1.opRevolve","SWEPT_FACE",FACE,{"disambiguationData":[OSD([subQ22]),TDD([makeQuery(id+"F0.imprint","IMPRINT",EDGE,{"disambiguationData":[TD([[makeQuery(id+"F0.imprint","INTERSECT",VERTEX,{"derivedFrom":[subQ22,subQ0]}),-1.0]])],"derivedFrom":subQ22})])]})})})})})})})})})});}
            var Q15;
            {var subQ0=sQuery(id+"F0.wireOp",EDGE,"E18");var subQ2=sQuery(id+"F12.wireOp",EDGE,"E63");var subQ3=sQuery(id+"F12.wireOp",EDGE,"E62");var subQ4=sQuery(id+"F12.wireOp",EDGE,"E61");var subQ5=sQuery(id+"F12.wireOp",EDGE,"E60.1");var subQ6=sQuery(id+"F12.wireOp",EDGE,"E60.0");var subQ7=sQuery(id+"F0.wireOp",EDGE,"E19");var subQ9=sQuery(id+"F9.wireOp",EDGE,"E59");var subQ10=sQuery(id+"F9.wireOp",EDGE,"E58");var subQ11=sQuery(id+"F9.wireOp",EDGE,"E57");var subQ12=sQuery(id+"F9.wireOp",EDGE,"E56");var subQ13=sQuery(id+"F9.wireOp",EDGE,"E55");var subQ14=makeQuery(id+"FgpSSfUhpf4qGKz_2.1.F10.opRevolve","CAP_FACE",FACE,{"disambiguationData":[OSD([subQ13,subQ12,subQ11,subQ10,subQ9])],"isStart":true});var subQ15=makeQuery(id+"F13.opRevolve","CAP_FACE",FACE,{"disambiguationData":[OSD([subQ6,subQ5,subQ4,subQ3,subQ2])],"isStart":true});var subQ21=sQuery(id+"F0.wireOp",EDGE,"E9");var subQ22=sQuery(id+"F0.wireOp",EDGE,"E0");var subQ23=makeQuery(id+"F3.opRevolve","CAP_FACE",FACE,{"disambiguationData":[OSD([subQ22,subQ21,subQ0,subQ7])],"isStart":true});Q15=makeQuery(id+"FgpSSfUhpf4qGKz_2.1.F13.boolean.opBoolean","SPLIT",FACE,{"disambiguationData":[TD([subQ14])],"derivedFrom":makeQuery(id+"FgpSSfUhpf4qGKz_2.1.F10.boolean.opBoolean","SPLIT",FACE,{"disambiguationData":[TD([subQ15])],"derivedFrom":makeQuery(id+"FgpSSfUhpf4qGKz_2.1.F7.boolean.opBoolean","SPLIT",FACE,{"disambiguationData":[TD([subQ15])],"derivedFrom":makeQuery(id+"FgpSSfUhpf4qGKz_2.1.F3.boolean.opBoolean","SPLIT",FACE,{"disambiguationData":[TD([makeQuery(id+"FgpSSfUhpf4qGKz_2.1.F3.opRevolve","CAP_FACE",FACE,{"disambiguationData":[OSD([subQ22,subQ21,subQ0,subQ7])],"isStart":false})])],"derivedFrom":makeQuery(id+"FeTh8RoejFn6YHX_2.1.F13.boolean.opBoolean","SPLIT",FACE,{"disambiguationData":[TD([subQ15])],"derivedFrom":makeQuery(id+"FeTh8RoejFn6YHX_2.1.F10.boolean.opBoolean","SPLIT",FACE,{"disambiguationData":[TD([subQ15])],"derivedFrom":makeQuery(id+"FeTh8RoejFn6YHX_2.1.F7.boolean.opBoolean","SPLIT",FACE,{"disambiguationData":[TD([subQ15])],"derivedFrom":makeQuery(id+"F13.boolean.opBoolean","SPLIT",FACE,{"disambiguationData":[TD([subQ23])],"derivedFrom":makeQuery(id+"F10.boolean.opBoolean","SPLIT",FACE,{"disambiguationData":[TD([subQ23])],"derivedFrom":makeQuery(id+"F7.boolean.opBoolean","SPLIT",FACE,{"disambiguationData":[TD([subQ23])],"derivedFrom":makeQuery(id+"F1.opRevolve","SWEPT_FACE",FACE,{"disambiguationData":[OSD([subQ22]),TDD([makeQuery(id+"F0.imprint","IMPRINT",EDGE,{"disambiguationData":[TD([[makeQuery(id+"F0.imprint","INTERSECT",VERTEX,{"derivedFrom":[subQ22,subQ0]}),-1.0]])],"derivedFrom":subQ22})])]})})})})})})})})})})});}
            var Q16;
            {var subQ0=sQuery(id+"F0.wireOp",EDGE,"E18");var subQ2=sQuery(id+"F0.wireOp",EDGE,"E19");var subQ4=sQuery(id+"F6.wireOp",EDGE,"E53");var subQ5=sQuery(id+"F6.wireOp",EDGE,"E52");var subQ6=sQuery(id+"F6.wireOp",EDGE,"E51");var subQ7=sQuery(id+"F6.wireOp",EDGE,"E50");var subQ8=sQuery(id+"F6.wireOp",EDGE,"E49.0");var subQ9=makeQuery(id+"FgpSSfUhpf4qGKz_2.1.F7.opRevolve","CAP_FACE",FACE,{"disambiguationData":[OSD([subQ8,subQ7,subQ6,subQ5,subQ4])],"isStart":false});var subQ15=sQuery(id+"F12.wireOp",EDGE,"E63");var subQ16=sQuery(id+"F12.wireOp",EDGE,"E62");var subQ17=sQuery(id+"F12.wireOp",EDGE,"E61");var subQ18=sQuery(id+"F12.wireOp",EDGE,"E60.1");var subQ19=sQuery(id+"F12.wireOp",EDGE,"E60.0");var subQ20=makeQuery(id+"F13.opRevolve","CAP_FACE",FACE,{"disambiguationData":[OSD([subQ19,subQ18,subQ17,subQ16,subQ15])],"isStart":true});var subQ21=sQuery(id+"F0.wireOp",EDGE,"E9");var subQ22=sQuery(id+"F0.wireOp",EDGE,"E0");var subQ23=makeQuery(id+"F3.opRevolve","CAP_FACE",FACE,{"disambiguationData":[OSD([subQ22,subQ21,subQ0,subQ2])],"isStart":true});Q16=makeQuery(id+"FgpSSfUhpf4qGKz_2.1.F10.boolean.opBoolean","SPLIT",FACE,{"disambiguationData":[TD([subQ9])],"derivedFrom":makeQuery(id+"FgpSSfUhpf4qGKz_2.1.F7.boolean.opBoolean","SPLIT",FACE,{"disambiguationData":[TD([subQ20])],"derivedFrom":makeQuery(id+"FgpSSfUhpf4qGKz_2.1.F3.boolean.opBoolean","SPLIT",FACE,{"disambiguationData":[TD([makeQuery(id+"FgpSSfUhpf4qGKz_2.1.F3.opRevolve","CAP_FACE",FACE,{"disambiguationData":[OSD([subQ22,subQ21,subQ0,subQ2])],"isStart":false})])],"derivedFrom":makeQuery(id+"FeTh8RoejFn6YHX_2.1.F13.boolean.opBoolean","SPLIT",FACE,{"disambiguationData":[TD([subQ20])],"derivedFrom":makeQuery(id+"FeTh8RoejFn6YHX_2.1.F10.boolean.opBoolean","SPLIT",FACE,{"disambiguationData":[TD([subQ20])],"derivedFrom":makeQuery(id+"FeTh8RoejFn6YHX_2.1.F7.boolean.opBoolean","SPLIT",FACE,{"disambiguationData":[TD([subQ20])],"derivedFrom":makeQuery(id+"F13.boolean.opBoolean","SPLIT",FACE,{"disambiguationData":[TD([subQ23])],"derivedFrom":makeQuery(id+"F10.boolean.opBoolean","SPLIT",FACE,{"disambiguationData":[TD([subQ23])],"derivedFrom":makeQuery(id+"F7.boolean.opBoolean","SPLIT",FACE,{"disambiguationData":[TD([subQ23])],"derivedFrom":makeQuery(id+"F1.opRevolve","SWEPT_FACE",FACE,{"disambiguationData":[OSD([subQ22]),TDD([makeQuery(id+"F0.imprint","IMPRINT",EDGE,{"disambiguationData":[TD([[makeQuery(id+"F0.imprint","INTERSECT",VERTEX,{"derivedFrom":[subQ22,subQ0]}),-1.0]])],"derivedFrom":subQ22})])]})})})})})})})})})});}
            var Q17;
            {var subQ0=sQuery(id+"F0.wireOp",EDGE,"E18");var subQ2=sQuery(id+"F0.wireOp",EDGE,"E19");var subQ4=sQuery(id+"F0.wireOp",EDGE,"E9");var subQ5=sQuery(id+"F0.wireOp",EDGE,"E0");var subQ6=makeQuery(id+"FgpSSfUhpf4qGKz_2.1.F3.opRevolve","CAP_FACE",FACE,{"disambiguationData":[OSD([subQ5,subQ4,subQ0,subQ2])],"isStart":false});var subQ12=sQuery(id+"F12.wireOp",EDGE,"E63");var subQ13=sQuery(id+"F12.wireOp",EDGE,"E62");var subQ14=sQuery(id+"F12.wireOp",EDGE,"E61");var subQ15=sQuery(id+"F12.wireOp",EDGE,"E60.1");var subQ16=sQuery(id+"F12.wireOp",EDGE,"E60.0");var subQ17=makeQuery(id+"F13.opRevolve","CAP_FACE",FACE,{"disambiguationData":[OSD([subQ16,subQ15,subQ14,subQ13,subQ12])],"isStart":true});var subQ23=makeQuery(id+"F3.opRevolve","CAP_FACE",FACE,{"disambiguationData":[OSD([subQ5,subQ4,subQ0,subQ2])],"isStart":true});Q17=makeQuery(id+"FgpSSfUhpf4qGKz_2.1.F7.boolean.opBoolean","SPLIT",FACE,{"disambiguationData":[TD([subQ6])],"derivedFrom":makeQuery(id+"FgpSSfUhpf4qGKz_2.1.F3.boolean.opBoolean","SPLIT",FACE,{"disambiguationData":[TD([subQ6])],"derivedFrom":makeQuery(id+"FeTh8RoejFn6YHX_2.1.F13.boolean.opBoolean","SPLIT",FACE,{"disambiguationData":[TD([subQ17])],"derivedFrom":makeQuery(id+"FeTh8RoejFn6YHX_2.1.F10.boolean.opBoolean","SPLIT",FACE,{"disambiguationData":[TD([subQ17])],"derivedFrom":makeQuery(id+"FeTh8RoejFn6YHX_2.1.F7.boolean.opBoolean","SPLIT",FACE,{"disambiguationData":[TD([subQ17])],"derivedFrom":makeQuery(id+"F13.boolean.opBoolean","SPLIT",FACE,{"disambiguationData":[TD([subQ23])],"derivedFrom":makeQuery(id+"F10.boolean.opBoolean","SPLIT",FACE,{"disambiguationData":[TD([subQ23])],"derivedFrom":makeQuery(id+"F7.boolean.opBoolean","SPLIT",FACE,{"disambiguationData":[TD([subQ23])],"derivedFrom":makeQuery(id+"F1.opRevolve","SWEPT_FACE",FACE,{"disambiguationData":[OSD([subQ5]),TDD([makeQuery(id+"F0.imprint","IMPRINT",EDGE,{"disambiguationData":[TD([[makeQuery(id+"F0.imprint","INTERSECT",VERTEX,{"derivedFrom":[subQ5,subQ0]}),-1.0]])],"derivedFrom":subQ5})])]})})})})})})})})});}
            var Q18;
            {var subQ0=sQuery(id+"F0.wireOp",EDGE,"E18");var subQ2=sQuery(id+"F0.wireOp",EDGE,"E19");var subQ3=sQuery(id+"F0.wireOp",EDGE,"E9");var subQ4=sQuery(id+"F0.wireOp",EDGE,"E0");var subQ5=makeQuery(id+"FgpSSfUhpf4qGKz_2.1.F3.opRevolve","CAP_FACE",FACE,{"disambiguationData":[OSD([subQ4,subQ3,subQ0,subQ2])],"isStart":true});var subQ12=sQuery(id+"F12.wireOp",EDGE,"E63");var subQ13=sQuery(id+"F12.wireOp",EDGE,"E62");var subQ14=sQuery(id+"F12.wireOp",EDGE,"E61");var subQ15=sQuery(id+"F12.wireOp",EDGE,"E60.1");var subQ16=sQuery(id+"F12.wireOp",EDGE,"E60.0");var subQ18=makeQuery(id+"F13.opRevolve","CAP_FACE",FACE,{"disambiguationData":[OSD([subQ16,subQ15,subQ14,subQ13,subQ12])],"isStart":true});var subQ24=makeQuery(id+"F3.opRevolve","CAP_FACE",FACE,{"disambiguationData":[OSD([subQ4,subQ3,subQ0,subQ2])],"isStart":true});Q18=makeQuery(id+"FgpSSfUhpf4qGKz_2.1.FeTh8RoejFn6YHX_2.1.F7.boolean.opBoolean","SPLIT",FACE,{"disambiguationData":[TD([subQ5])],"derivedFrom":makeQuery(id+"FgpSSfUhpf4qGKz_2.1.F3.boolean.opBoolean","SPLIT",FACE,{"disambiguationData":[TD([subQ5])],"derivedFrom":makeQuery(id+"FeTh8RoejFn6YHX_2.1.F13.boolean.opBoolean","SPLIT",FACE,{"disambiguationData":[TD([subQ18])],"derivedFrom":makeQuery(id+"FeTh8RoejFn6YHX_2.1.F10.boolean.opBoolean","SPLIT",FACE,{"disambiguationData":[TD([subQ18])],"derivedFrom":makeQuery(id+"FeTh8RoejFn6YHX_2.1.F7.boolean.opBoolean","SPLIT",FACE,{"disambiguationData":[TD([subQ18])],"derivedFrom":makeQuery(id+"F13.boolean.opBoolean","SPLIT",FACE,{"disambiguationData":[TD([subQ24])],"derivedFrom":makeQuery(id+"F10.boolean.opBoolean","SPLIT",FACE,{"disambiguationData":[TD([subQ24])],"derivedFrom":makeQuery(id+"F7.boolean.opBoolean","SPLIT",FACE,{"disambiguationData":[TD([subQ24])],"derivedFrom":makeQuery(id+"F1.opRevolve","SWEPT_FACE",FACE,{"disambiguationData":[OSD([subQ4]),TDD([makeQuery(id+"F0.imprint","IMPRINT",EDGE,{"disambiguationData":[TD([[makeQuery(id+"F0.imprint","INTERSECT",VERTEX,{"derivedFrom":[subQ4,subQ0]}),-1.0]])],"derivedFrom":subQ4})])]})})})})})})})})});}
            var Q19;
            {var subQ0=sQuery(id+"F0.wireOp",EDGE,"E18");var subQ2=sQuery(id+"F0.wireOp",EDGE,"E19");var subQ4=sQuery(id+"F12.wireOp",EDGE,"E63");var subQ5=sQuery(id+"F12.wireOp",EDGE,"E62");var subQ6=sQuery(id+"F12.wireOp",EDGE,"E61");var subQ7=sQuery(id+"F12.wireOp",EDGE,"E60.1");var subQ8=sQuery(id+"F12.wireOp",EDGE,"E60.0");var subQ9=makeQuery(id+"F13.opRevolve","CAP_FACE",FACE,{"disambiguationData":[OSD([subQ8,subQ7,subQ6,subQ5,subQ4])],"isStart":true});var subQ20=sQuery(id+"F0.wireOp",EDGE,"E9");var subQ21=sQuery(id+"F0.wireOp",EDGE,"E0");var subQ22=makeQuery(id+"F3.opRevolve","CAP_FACE",FACE,{"disambiguationData":[OSD([subQ21,subQ20,subQ0,subQ2])],"isStart":true});Q19=makeQuery(id+"FgpSSfUhpf4qGKz_2.1.F13.boolean.opBoolean","SPLIT",FACE,{"disambiguationData":[TD([subQ9])],"derivedFrom":makeQuery(id+"FgpSSfUhpf4qGKz_2.1.F10.boolean.opBoolean","SPLIT",FACE,{"disambiguationData":[TD([subQ9])],"derivedFrom":makeQuery(id+"FgpSSfUhpf4qGKz_2.1.F7.boolean.opBoolean","SPLIT",FACE,{"disambiguationData":[TD([subQ9])],"derivedFrom":makeQuery(id+"FgpSSfUhpf4qGKz_2.1.F3.boolean.opBoolean","SPLIT",FACE,{"disambiguationData":[TD([makeQuery(id+"FgpSSfUhpf4qGKz_2.1.F3.opRevolve","CAP_FACE",FACE,{"disambiguationData":[OSD([subQ21,subQ20,subQ0,subQ2])],"isStart":false})])],"derivedFrom":makeQuery(id+"FeTh8RoejFn6YHX_2.1.F13.boolean.opBoolean","SPLIT",FACE,{"disambiguationData":[TD([subQ9])],"derivedFrom":makeQuery(id+"FeTh8RoejFn6YHX_2.1.F10.boolean.opBoolean","SPLIT",FACE,{"disambiguationData":[TD([subQ9])],"derivedFrom":makeQuery(id+"FeTh8RoejFn6YHX_2.1.F7.boolean.opBoolean","SPLIT",FACE,{"disambiguationData":[TD([subQ9])],"derivedFrom":makeQuery(id+"F13.boolean.opBoolean","SPLIT",FACE,{"disambiguationData":[TD([subQ22])],"derivedFrom":makeQuery(id+"F10.boolean.opBoolean","SPLIT",FACE,{"disambiguationData":[TD([subQ22])],"derivedFrom":makeQuery(id+"F7.boolean.opBoolean","SPLIT",FACE,{"disambiguationData":[TD([subQ22])],"derivedFrom":makeQuery(id+"F1.opRevolve","SWEPT_FACE",FACE,{"disambiguationData":[OSD([subQ21]),TDD([makeQuery(id+"F0.imprint","IMPRINT",EDGE,{"disambiguationData":[TD([[makeQuery(id+"F0.imprint","INTERSECT",VERTEX,{"derivedFrom":[subQ21,subQ0]}),-1.0]])],"derivedFrom":subQ21})])]})})})})})})})})})})});}
            var Q20;
            {var subQ0=sQuery(id+"F0.wireOp",EDGE,"E15");var subQ2=sQuery(id+"F0.wireOp",EDGE,"E17");var subQ4=sQuery(id+"F12.wireOp",EDGE,"E63");var subQ5=sQuery(id+"F12.wireOp",EDGE,"E62");var subQ6=sQuery(id+"F12.wireOp",EDGE,"E61");var subQ7=sQuery(id+"F12.wireOp",EDGE,"E60.1");var subQ8=sQuery(id+"F12.wireOp",EDGE,"E60.0");var subQ9=makeQuery(id+"F13.opRevolve","CAP_FACE",FACE,{"disambiguationData":[OSD([subQ8,subQ7,subQ6,subQ5,subQ4])],"isStart":true});var subQ20=sQuery(id+"F0.wireOp",EDGE,"E9");var subQ21=sQuery(id+"F0.wireOp",EDGE,"E0");var subQ22=makeQuery(id+"F3.opRevolve","CAP_FACE",FACE,{"disambiguationData":[OSD([subQ21,subQ20,subQ0,subQ2])],"isStart":true});Q20=makeQuery(id+"FgpSSfUhpf4qGKz_2.1.F13.boolean.opBoolean","SPLIT",FACE,{"disambiguationData":[TD([subQ9])],"derivedFrom":makeQuery(id+"FgpSSfUhpf4qGKz_2.1.F10.boolean.opBoolean","SPLIT",FACE,{"disambiguationData":[TD([subQ9])],"derivedFrom":makeQuery(id+"FgpSSfUhpf4qGKz_2.1.F7.boolean.opBoolean","SPLIT",FACE,{"disambiguationData":[TD([subQ9])],"derivedFrom":makeQuery(id+"FgpSSfUhpf4qGKz_2.1.F3.boolean.opBoolean","SPLIT",FACE,{"disambiguationData":[TD([makeQuery(id+"FgpSSfUhpf4qGKz_2.1.F3.opRevolve","CAP_FACE",FACE,{"disambiguationData":[OSD([subQ21,subQ20,subQ0,subQ2])],"isStart":false})])],"derivedFrom":makeQuery(id+"FeTh8RoejFn6YHX_2.1.F13.boolean.opBoolean","SPLIT",FACE,{"disambiguationData":[TD([subQ9])],"derivedFrom":makeQuery(id+"FeTh8RoejFn6YHX_2.1.F10.boolean.opBoolean","SPLIT",FACE,{"disambiguationData":[TD([subQ9])],"derivedFrom":makeQuery(id+"FeTh8RoejFn6YHX_2.1.F7.boolean.opBoolean","SPLIT",FACE,{"disambiguationData":[TD([subQ9])],"derivedFrom":makeQuery(id+"F13.boolean.opBoolean","SPLIT",FACE,{"disambiguationData":[TD([subQ22])],"derivedFrom":makeQuery(id+"F10.boolean.opBoolean","SPLIT",FACE,{"disambiguationData":[TD([subQ22])],"derivedFrom":makeQuery(id+"F7.boolean.opBoolean","SPLIT",FACE,{"disambiguationData":[TD([subQ22])],"derivedFrom":makeQuery(id+"F1.opRevolve","SWEPT_FACE",FACE,{"disambiguationData":[OSD([subQ21]),TDD([makeQuery(id+"F0.imprint","IMPRINT",EDGE,{"disambiguationData":[TD([[makeQuery(id+"F0.imprint","INTERSECT",VERTEX,{"derivedFrom":[subQ21,subQ0]}),-1.0]])],"derivedFrom":subQ21})])]})})})})})})})})})})});}
            var Q21;
            {var subQ0=sQuery(id+"F0.wireOp",EDGE,"E15");var subQ2=sQuery(id+"F0.wireOp",EDGE,"E17");var subQ4=sQuery(id+"F9.wireOp",EDGE,"E59");var subQ5=sQuery(id+"F9.wireOp",EDGE,"E58");var subQ6=sQuery(id+"F9.wireOp",EDGE,"E57");var subQ7=sQuery(id+"F9.wireOp",EDGE,"E56");var subQ8=sQuery(id+"F9.wireOp",EDGE,"E55");var subQ9=makeQuery(id+"FgpSSfUhpf4qGKz_2.1.F10.opRevolve","CAP_FACE",FACE,{"disambiguationData":[OSD([subQ8,subQ7,subQ6,subQ5,subQ4])],"isStart":true});var subQ10=sQuery(id+"F12.wireOp",EDGE,"E63");var subQ11=sQuery(id+"F12.wireOp",EDGE,"E62");var subQ12=sQuery(id+"F12.wireOp",EDGE,"E61");var subQ13=sQuery(id+"F12.wireOp",EDGE,"E60.1");var subQ14=sQuery(id+"F12.wireOp",EDGE,"E60.0");var subQ15=makeQuery(id+"F13.opRevolve","CAP_FACE",FACE,{"disambiguationData":[OSD([subQ14,subQ13,subQ12,subQ11,subQ10])],"isStart":true});var subQ21=sQuery(id+"F0.wireOp",EDGE,"E9");var subQ22=sQuery(id+"F0.wireOp",EDGE,"E0");var subQ23=makeQuery(id+"F3.opRevolve","CAP_FACE",FACE,{"disambiguationData":[OSD([subQ22,subQ21,subQ0,subQ2])],"isStart":true});Q21=makeQuery(id+"FgpSSfUhpf4qGKz_2.1.F13.boolean.opBoolean","SPLIT",FACE,{"disambiguationData":[TD([subQ9])],"derivedFrom":makeQuery(id+"FgpSSfUhpf4qGKz_2.1.F10.boolean.opBoolean","SPLIT",FACE,{"disambiguationData":[TD([subQ15])],"derivedFrom":makeQuery(id+"FgpSSfUhpf4qGKz_2.1.F7.boolean.opBoolean","SPLIT",FACE,{"disambiguationData":[TD([subQ15])],"derivedFrom":makeQuery(id+"FgpSSfUhpf4qGKz_2.1.F3.boolean.opBoolean","SPLIT",FACE,{"disambiguationData":[TD([makeQuery(id+"FgpSSfUhpf4qGKz_2.1.F3.opRevolve","CAP_FACE",FACE,{"disambiguationData":[OSD([subQ22,subQ21,subQ0,subQ2])],"isStart":false})])],"derivedFrom":makeQuery(id+"FeTh8RoejFn6YHX_2.1.F13.boolean.opBoolean","SPLIT",FACE,{"disambiguationData":[TD([subQ15])],"derivedFrom":makeQuery(id+"FeTh8RoejFn6YHX_2.1.F10.boolean.opBoolean","SPLIT",FACE,{"disambiguationData":[TD([subQ15])],"derivedFrom":makeQuery(id+"FeTh8RoejFn6YHX_2.1.F7.boolean.opBoolean","SPLIT",FACE,{"disambiguationData":[TD([subQ15])],"derivedFrom":makeQuery(id+"F13.boolean.opBoolean","SPLIT",FACE,{"disambiguationData":[TD([subQ23])],"derivedFrom":makeQuery(id+"F10.boolean.opBoolean","SPLIT",FACE,{"disambiguationData":[TD([subQ23])],"derivedFrom":makeQuery(id+"F7.boolean.opBoolean","SPLIT",FACE,{"disambiguationData":[TD([subQ23])],"derivedFrom":makeQuery(id+"F1.opRevolve","SWEPT_FACE",FACE,{"disambiguationData":[OSD([subQ22]),TDD([makeQuery(id+"F0.imprint","IMPRINT",EDGE,{"disambiguationData":[TD([[makeQuery(id+"F0.imprint","INTERSECT",VERTEX,{"derivedFrom":[subQ22,subQ0]}),-1.0]])],"derivedFrom":subQ22})])]})})})})})})})})})})});}
            var Q22;
            {var subQ0=sQuery(id+"F0.wireOp",EDGE,"E13");var subQ2=sQuery(id+"F9.wireOp",EDGE,"E59");var subQ3=sQuery(id+"F9.wireOp",EDGE,"E58");var subQ4=sQuery(id+"F9.wireOp",EDGE,"E57");var subQ5=sQuery(id+"F9.wireOp",EDGE,"E56");var subQ6=sQuery(id+"F9.wireOp",EDGE,"E55");var subQ7=makeQuery(id+"FgpSSfUhpf4qGKz_2.1.F10.opRevolve","CAP_FACE",FACE,{"disambiguationData":[OSD([subQ6,subQ5,subQ4,subQ3,subQ2])],"isStart":true});var subQ8=sQuery(id+"F0.wireOp",EDGE,"E14");var subQ10=sQuery(id+"F12.wireOp",EDGE,"E63");var subQ11=sQuery(id+"F12.wireOp",EDGE,"E62");var subQ12=sQuery(id+"F12.wireOp",EDGE,"E61");var subQ13=sQuery(id+"F12.wireOp",EDGE,"E60.1");var subQ14=sQuery(id+"F12.wireOp",EDGE,"E60.0");var subQ15=makeQuery(id+"F13.opRevolve","CAP_FACE",FACE,{"disambiguationData":[OSD([subQ14,subQ13,subQ12,subQ11,subQ10])],"isStart":true});var subQ21=sQuery(id+"F0.wireOp",EDGE,"E9");var subQ22=sQuery(id+"F0.wireOp",EDGE,"E0");var subQ23=makeQuery(id+"F3.opRevolve","CAP_FACE",FACE,{"disambiguationData":[OSD([subQ22,subQ21,subQ0,subQ8])],"isStart":true});Q22=makeQuery(id+"FgpSSfUhpf4qGKz_2.1.F13.boolean.opBoolean","SPLIT",FACE,{"disambiguationData":[TD([subQ7])],"derivedFrom":makeQuery(id+"FgpSSfUhpf4qGKz_2.1.F10.boolean.opBoolean","SPLIT",FACE,{"disambiguationData":[TD([subQ15])],"derivedFrom":makeQuery(id+"FgpSSfUhpf4qGKz_2.1.F7.boolean.opBoolean","SPLIT",FACE,{"disambiguationData":[TD([subQ15])],"derivedFrom":makeQuery(id+"FgpSSfUhpf4qGKz_2.1.F3.boolean.opBoolean","SPLIT",FACE,{"disambiguationData":[TD([makeQuery(id+"FgpSSfUhpf4qGKz_2.1.F3.opRevolve","CAP_FACE",FACE,{"disambiguationData":[OSD([subQ22,subQ21,subQ0,subQ8])],"isStart":false})])],"derivedFrom":makeQuery(id+"FeTh8RoejFn6YHX_2.1.F13.boolean.opBoolean","SPLIT",FACE,{"disambiguationData":[TD([subQ15])],"derivedFrom":makeQuery(id+"FeTh8RoejFn6YHX_2.1.F10.boolean.opBoolean","SPLIT",FACE,{"disambiguationData":[TD([subQ15])],"derivedFrom":makeQuery(id+"FeTh8RoejFn6YHX_2.1.F7.boolean.opBoolean","SPLIT",FACE,{"disambiguationData":[TD([subQ15])],"derivedFrom":makeQuery(id+"F13.boolean.opBoolean","SPLIT",FACE,{"disambiguationData":[TD([subQ23])],"derivedFrom":makeQuery(id+"F10.boolean.opBoolean","SPLIT",FACE,{"disambiguationData":[TD([subQ23])],"derivedFrom":makeQuery(id+"F7.boolean.opBoolean","SPLIT",FACE,{"disambiguationData":[TD([subQ23])],"derivedFrom":makeQuery(id+"F1.opRevolve","SWEPT_FACE",FACE,{"disambiguationData":[OSD([subQ22]),TDD([makeQuery(id+"F0.imprint","IMPRINT",EDGE,{"disambiguationData":[TD([[makeQuery(id+"F0.imprint","INTERSECT",VERTEX,{"derivedFrom":[subQ22,subQ0]}),-1.0]])],"derivedFrom":subQ22})])]})})})})})})})})})})});}
            var Q23;
            {var subQ0=sQuery(id+"F0.wireOp",EDGE,"E13");var subQ2=sQuery(id+"F0.wireOp",EDGE,"E14");var subQ4=sQuery(id+"F12.wireOp",EDGE,"E63");var subQ5=sQuery(id+"F12.wireOp",EDGE,"E62");var subQ6=sQuery(id+"F12.wireOp",EDGE,"E61");var subQ7=sQuery(id+"F12.wireOp",EDGE,"E60.1");var subQ8=sQuery(id+"F12.wireOp",EDGE,"E60.0");var subQ9=makeQuery(id+"F13.opRevolve","CAP_FACE",FACE,{"disambiguationData":[OSD([subQ8,subQ7,subQ6,subQ5,subQ4])],"isStart":true});var subQ20=sQuery(id+"F0.wireOp",EDGE,"E9");var subQ21=sQuery(id+"F0.wireOp",EDGE,"E0");var subQ22=makeQuery(id+"F3.opRevolve","CAP_FACE",FACE,{"disambiguationData":[OSD([subQ21,subQ20,subQ0,subQ2])],"isStart":true});Q23=makeQuery(id+"FgpSSfUhpf4qGKz_2.1.F13.boolean.opBoolean","SPLIT",FACE,{"disambiguationData":[TD([subQ9])],"derivedFrom":makeQuery(id+"FgpSSfUhpf4qGKz_2.1.F10.boolean.opBoolean","SPLIT",FACE,{"disambiguationData":[TD([subQ9])],"derivedFrom":makeQuery(id+"FgpSSfUhpf4qGKz_2.1.F7.boolean.opBoolean","SPLIT",FACE,{"disambiguationData":[TD([subQ9])],"derivedFrom":makeQuery(id+"FgpSSfUhpf4qGKz_2.1.F3.boolean.opBoolean","SPLIT",FACE,{"disambiguationData":[TD([makeQuery(id+"FgpSSfUhpf4qGKz_2.1.F3.opRevolve","CAP_FACE",FACE,{"disambiguationData":[OSD([subQ21,subQ20,subQ0,subQ2])],"isStart":false})])],"derivedFrom":makeQuery(id+"FeTh8RoejFn6YHX_2.1.F13.boolean.opBoolean","SPLIT",FACE,{"disambiguationData":[TD([subQ9])],"derivedFrom":makeQuery(id+"FeTh8RoejFn6YHX_2.1.F10.boolean.opBoolean","SPLIT",FACE,{"disambiguationData":[TD([subQ9])],"derivedFrom":makeQuery(id+"FeTh8RoejFn6YHX_2.1.F7.boolean.opBoolean","SPLIT",FACE,{"disambiguationData":[TD([subQ9])],"derivedFrom":makeQuery(id+"F13.boolean.opBoolean","SPLIT",FACE,{"disambiguationData":[TD([subQ22])],"derivedFrom":makeQuery(id+"F10.boolean.opBoolean","SPLIT",FACE,{"disambiguationData":[TD([subQ22])],"derivedFrom":makeQuery(id+"F7.boolean.opBoolean","SPLIT",FACE,{"disambiguationData":[TD([subQ22])],"derivedFrom":makeQuery(id+"F1.opRevolve","SWEPT_FACE",FACE,{"disambiguationData":[OSD([subQ21]),TDD([makeQuery(id+"F0.imprint","IMPRINT",EDGE,{"disambiguationData":[TD([[makeQuery(id+"F0.imprint","INTERSECT",VERTEX,{"derivedFrom":[subQ21,subQ0]}),-1.0]])],"derivedFrom":subQ21})])]})})})})})})})})})})});}
            var Q24;
            {var subQ0=sQuery(id+"F0.wireOp",EDGE,"E15");var subQ2=sQuery(id+"F0.wireOp",EDGE,"E17");var subQ4=sQuery(id+"F6.wireOp",EDGE,"E53");var subQ5=sQuery(id+"F6.wireOp",EDGE,"E52");var subQ6=sQuery(id+"F6.wireOp",EDGE,"E51");var subQ7=sQuery(id+"F6.wireOp",EDGE,"E50");var subQ8=sQuery(id+"F6.wireOp",EDGE,"E49.0");var subQ9=makeQuery(id+"FgpSSfUhpf4qGKz_2.1.F7.opRevolve","CAP_FACE",FACE,{"disambiguationData":[OSD([subQ8,subQ7,subQ6,subQ5,subQ4])],"isStart":false});var subQ15=sQuery(id+"F12.wireOp",EDGE,"E63");var subQ16=sQuery(id+"F12.wireOp",EDGE,"E62");var subQ17=sQuery(id+"F12.wireOp",EDGE,"E61");var subQ18=sQuery(id+"F12.wireOp",EDGE,"E60.1");var subQ19=sQuery(id+"F12.wireOp",EDGE,"E60.0");var subQ20=makeQuery(id+"F13.opRevolve","CAP_FACE",FACE,{"disambiguationData":[OSD([subQ19,subQ18,subQ17,subQ16,subQ15])],"isStart":true});var subQ21=sQuery(id+"F0.wireOp",EDGE,"E9");var subQ22=sQuery(id+"F0.wireOp",EDGE,"E0");var subQ23=makeQuery(id+"F3.opRevolve","CAP_FACE",FACE,{"disambiguationData":[OSD([subQ22,subQ21,subQ0,subQ2])],"isStart":true});Q24=makeQuery(id+"FgpSSfUhpf4qGKz_2.1.F10.boolean.opBoolean","SPLIT",FACE,{"disambiguationData":[TD([subQ9])],"derivedFrom":makeQuery(id+"FgpSSfUhpf4qGKz_2.1.F7.boolean.opBoolean","SPLIT",FACE,{"disambiguationData":[TD([subQ20])],"derivedFrom":makeQuery(id+"FgpSSfUhpf4qGKz_2.1.F3.boolean.opBoolean","SPLIT",FACE,{"disambiguationData":[TD([makeQuery(id+"FgpSSfUhpf4qGKz_2.1.F3.opRevolve","CAP_FACE",FACE,{"disambiguationData":[OSD([subQ22,subQ21,subQ0,subQ2])],"isStart":false})])],"derivedFrom":makeQuery(id+"FeTh8RoejFn6YHX_2.1.F13.boolean.opBoolean","SPLIT",FACE,{"disambiguationData":[TD([subQ20])],"derivedFrom":makeQuery(id+"FeTh8RoejFn6YHX_2.1.F10.boolean.opBoolean","SPLIT",FACE,{"disambiguationData":[TD([subQ20])],"derivedFrom":makeQuery(id+"FeTh8RoejFn6YHX_2.1.F7.boolean.opBoolean","SPLIT",FACE,{"disambiguationData":[TD([subQ20])],"derivedFrom":makeQuery(id+"F13.boolean.opBoolean","SPLIT",FACE,{"disambiguationData":[TD([subQ23])],"derivedFrom":makeQuery(id+"F10.boolean.opBoolean","SPLIT",FACE,{"disambiguationData":[TD([subQ23])],"derivedFrom":makeQuery(id+"F7.boolean.opBoolean","SPLIT",FACE,{"disambiguationData":[TD([subQ23])],"derivedFrom":makeQuery(id+"F1.opRevolve","SWEPT_FACE",FACE,{"disambiguationData":[OSD([subQ22]),TDD([makeQuery(id+"F0.imprint","IMPRINT",EDGE,{"disambiguationData":[TD([[makeQuery(id+"F0.imprint","INTERSECT",VERTEX,{"derivedFrom":[subQ22,subQ0]}),-1.0]])],"derivedFrom":subQ22})])]})})})})})})})})})});}
            var Q25;
            {var subQ0=sQuery(id+"F0.wireOp",EDGE,"E15");var subQ7=sQuery(id+"F0.wireOp",EDGE,"E17");var subQ9=sQuery(id+"F0.wireOp",EDGE,"E9");var subQ10=sQuery(id+"F0.wireOp",EDGE,"E0");var subQ11=makeQuery(id+"FgpSSfUhpf4qGKz_2.1.F3.opRevolve","CAP_FACE",FACE,{"disambiguationData":[OSD([subQ10,subQ9,subQ0,subQ7])],"isStart":false});var subQ12=sQuery(id+"F12.wireOp",EDGE,"E63");var subQ13=sQuery(id+"F12.wireOp",EDGE,"E62");var subQ14=sQuery(id+"F12.wireOp",EDGE,"E61");var subQ15=sQuery(id+"F12.wireOp",EDGE,"E60.1");var subQ16=sQuery(id+"F12.wireOp",EDGE,"E60.0");var subQ17=makeQuery(id+"F13.opRevolve","CAP_FACE",FACE,{"disambiguationData":[OSD([subQ16,subQ15,subQ14,subQ13,subQ12])],"isStart":true});var subQ23=makeQuery(id+"F3.opRevolve","CAP_FACE",FACE,{"disambiguationData":[OSD([subQ10,subQ9,subQ0,subQ7])],"isStart":true});Q25=makeQuery(id+"FgpSSfUhpf4qGKz_2.1.F7.boolean.opBoolean","SPLIT",FACE,{"disambiguationData":[TD([subQ11])],"derivedFrom":makeQuery(id+"FgpSSfUhpf4qGKz_2.1.F3.boolean.opBoolean","SPLIT",FACE,{"disambiguationData":[TD([subQ11])],"derivedFrom":makeQuery(id+"FeTh8RoejFn6YHX_2.1.F13.boolean.opBoolean","SPLIT",FACE,{"disambiguationData":[TD([subQ17])],"derivedFrom":makeQuery(id+"FeTh8RoejFn6YHX_2.1.F10.boolean.opBoolean","SPLIT",FACE,{"disambiguationData":[TD([subQ17])],"derivedFrom":makeQuery(id+"FeTh8RoejFn6YHX_2.1.F7.boolean.opBoolean","SPLIT",FACE,{"disambiguationData":[TD([subQ17])],"derivedFrom":makeQuery(id+"F13.boolean.opBoolean","SPLIT",FACE,{"disambiguationData":[TD([subQ23])],"derivedFrom":makeQuery(id+"F10.boolean.opBoolean","SPLIT",FACE,{"disambiguationData":[TD([subQ23])],"derivedFrom":makeQuery(id+"F7.boolean.opBoolean","SPLIT",FACE,{"disambiguationData":[TD([subQ23])],"derivedFrom":makeQuery(id+"F1.opRevolve","SWEPT_FACE",FACE,{"disambiguationData":[OSD([subQ10]),TDD([makeQuery(id+"F0.imprint","IMPRINT",EDGE,{"disambiguationData":[TD([[makeQuery(id+"F0.imprint","INTERSECT",VERTEX,{"derivedFrom":[subQ10,subQ0]}),-1.0]])],"derivedFrom":subQ10})])]})})})})})})})})});}
            var Q26;
            {var subQ0=sQuery(id+"F0.wireOp",EDGE,"E13");var subQ2=sQuery(id+"F0.wireOp",EDGE,"E14");var subQ9=sQuery(id+"F6.wireOp",EDGE,"E53");var subQ10=sQuery(id+"F6.wireOp",EDGE,"E52");var subQ11=sQuery(id+"F6.wireOp",EDGE,"E51");var subQ12=sQuery(id+"F6.wireOp",EDGE,"E50");var subQ13=sQuery(id+"F6.wireOp",EDGE,"E49.0");var subQ14=makeQuery(id+"FgpSSfUhpf4qGKz_2.1.F7.opRevolve","CAP_FACE",FACE,{"disambiguationData":[OSD([subQ13,subQ12,subQ11,subQ10,subQ9])],"isStart":false});var subQ15=sQuery(id+"F12.wireOp",EDGE,"E63");var subQ16=sQuery(id+"F12.wireOp",EDGE,"E62");var subQ17=sQuery(id+"F12.wireOp",EDGE,"E61");var subQ18=sQuery(id+"F12.wireOp",EDGE,"E60.1");var subQ19=sQuery(id+"F12.wireOp",EDGE,"E60.0");var subQ20=makeQuery(id+"F13.opRevolve","CAP_FACE",FACE,{"disambiguationData":[OSD([subQ19,subQ18,subQ17,subQ16,subQ15])],"isStart":true});var subQ21=sQuery(id+"F0.wireOp",EDGE,"E9");var subQ22=sQuery(id+"F0.wireOp",EDGE,"E0");var subQ23=makeQuery(id+"F3.opRevolve","CAP_FACE",FACE,{"disambiguationData":[OSD([subQ22,subQ21,subQ0,subQ2])],"isStart":true});Q26=makeQuery(id+"FgpSSfUhpf4qGKz_2.1.F10.boolean.opBoolean","SPLIT",FACE,{"disambiguationData":[TD([subQ14])],"derivedFrom":makeQuery(id+"FgpSSfUhpf4qGKz_2.1.F7.boolean.opBoolean","SPLIT",FACE,{"disambiguationData":[TD([subQ20])],"derivedFrom":makeQuery(id+"FgpSSfUhpf4qGKz_2.1.F3.boolean.opBoolean","SPLIT",FACE,{"disambiguationData":[TD([makeQuery(id+"FgpSSfUhpf4qGKz_2.1.F3.opRevolve","CAP_FACE",FACE,{"disambiguationData":[OSD([subQ22,subQ21,subQ0,subQ2])],"isStart":false})])],"derivedFrom":makeQuery(id+"FeTh8RoejFn6YHX_2.1.F13.boolean.opBoolean","SPLIT",FACE,{"disambiguationData":[TD([subQ20])],"derivedFrom":makeQuery(id+"FeTh8RoejFn6YHX_2.1.F10.boolean.opBoolean","SPLIT",FACE,{"disambiguationData":[TD([subQ20])],"derivedFrom":makeQuery(id+"FeTh8RoejFn6YHX_2.1.F7.boolean.opBoolean","SPLIT",FACE,{"disambiguationData":[TD([subQ20])],"derivedFrom":makeQuery(id+"F13.boolean.opBoolean","SPLIT",FACE,{"disambiguationData":[TD([subQ23])],"derivedFrom":makeQuery(id+"F10.boolean.opBoolean","SPLIT",FACE,{"disambiguationData":[TD([subQ23])],"derivedFrom":makeQuery(id+"F7.boolean.opBoolean","SPLIT",FACE,{"disambiguationData":[TD([subQ23])],"derivedFrom":makeQuery(id+"F1.opRevolve","SWEPT_FACE",FACE,{"disambiguationData":[OSD([subQ22]),TDD([makeQuery(id+"F0.imprint","IMPRINT",EDGE,{"disambiguationData":[TD([[makeQuery(id+"F0.imprint","INTERSECT",VERTEX,{"derivedFrom":[subQ22,subQ0]}),-1.0]])],"derivedFrom":subQ22})])]})})})})})})})})})});}
            var Q27;
            {var subQ0=sQuery(id+"F0.wireOp",EDGE,"E13");var subQ2=sQuery(id+"F0.wireOp",EDGE,"E14");var subQ4=sQuery(id+"F0.wireOp",EDGE,"E9");var subQ5=sQuery(id+"F0.wireOp",EDGE,"E0");var subQ6=makeQuery(id+"FgpSSfUhpf4qGKz_2.1.F3.opRevolve","CAP_FACE",FACE,{"disambiguationData":[OSD([subQ5,subQ4,subQ0,subQ2])],"isStart":false});var subQ12=sQuery(id+"F12.wireOp",EDGE,"E63");var subQ13=sQuery(id+"F12.wireOp",EDGE,"E62");var subQ14=sQuery(id+"F12.wireOp",EDGE,"E61");var subQ15=sQuery(id+"F12.wireOp",EDGE,"E60.1");var subQ16=sQuery(id+"F12.wireOp",EDGE,"E60.0");var subQ17=makeQuery(id+"F13.opRevolve","CAP_FACE",FACE,{"disambiguationData":[OSD([subQ16,subQ15,subQ14,subQ13,subQ12])],"isStart":true});var subQ23=makeQuery(id+"F3.opRevolve","CAP_FACE",FACE,{"disambiguationData":[OSD([subQ5,subQ4,subQ0,subQ2])],"isStart":true});Q27=makeQuery(id+"FgpSSfUhpf4qGKz_2.1.F7.boolean.opBoolean","SPLIT",FACE,{"disambiguationData":[TD([subQ6])],"derivedFrom":makeQuery(id+"FgpSSfUhpf4qGKz_2.1.F3.boolean.opBoolean","SPLIT",FACE,{"disambiguationData":[TD([subQ6])],"derivedFrom":makeQuery(id+"FeTh8RoejFn6YHX_2.1.F13.boolean.opBoolean","SPLIT",FACE,{"disambiguationData":[TD([subQ17])],"derivedFrom":makeQuery(id+"FeTh8RoejFn6YHX_2.1.F10.boolean.opBoolean","SPLIT",FACE,{"disambiguationData":[TD([subQ17])],"derivedFrom":makeQuery(id+"FeTh8RoejFn6YHX_2.1.F7.boolean.opBoolean","SPLIT",FACE,{"disambiguationData":[TD([subQ17])],"derivedFrom":makeQuery(id+"F13.boolean.opBoolean","SPLIT",FACE,{"disambiguationData":[TD([subQ23])],"derivedFrom":makeQuery(id+"F10.boolean.opBoolean","SPLIT",FACE,{"disambiguationData":[TD([subQ23])],"derivedFrom":makeQuery(id+"F7.boolean.opBoolean","SPLIT",FACE,{"disambiguationData":[TD([subQ23])],"derivedFrom":makeQuery(id+"F1.opRevolve","SWEPT_FACE",FACE,{"disambiguationData":[OSD([subQ5]),TDD([makeQuery(id+"F0.imprint","IMPRINT",EDGE,{"disambiguationData":[TD([[makeQuery(id+"F0.imprint","INTERSECT",VERTEX,{"derivedFrom":[subQ5,subQ0]}),-1.0]])],"derivedFrom":subQ5})])]})})})})})})})})});}
            var Q28;
            {var subQ0=sQuery(id+"F0.wireOp",EDGE,"E13");var subQ2=sQuery(id+"F0.wireOp",EDGE,"E14");var subQ9=sQuery(id+"F0.wireOp",EDGE,"E9");var subQ10=sQuery(id+"F0.wireOp",EDGE,"E0");var subQ11=makeQuery(id+"FgpSSfUhpf4qGKz_2.1.F3.opRevolve","CAP_FACE",FACE,{"disambiguationData":[OSD([subQ10,subQ9,subQ0,subQ2])],"isStart":true});var subQ12=sQuery(id+"F12.wireOp",EDGE,"E63");var subQ13=sQuery(id+"F12.wireOp",EDGE,"E62");var subQ14=sQuery(id+"F12.wireOp",EDGE,"E61");var subQ15=sQuery(id+"F12.wireOp",EDGE,"E60.1");var subQ16=sQuery(id+"F12.wireOp",EDGE,"E60.0");var subQ18=makeQuery(id+"F13.opRevolve","CAP_FACE",FACE,{"disambiguationData":[OSD([subQ16,subQ15,subQ14,subQ13,subQ12])],"isStart":true});var subQ24=makeQuery(id+"F3.opRevolve","CAP_FACE",FACE,{"disambiguationData":[OSD([subQ10,subQ9,subQ0,subQ2])],"isStart":true});Q28=makeQuery(id+"FgpSSfUhpf4qGKz_2.1.FeTh8RoejFn6YHX_2.1.F7.boolean.opBoolean","SPLIT",FACE,{"disambiguationData":[TD([subQ11])],"derivedFrom":makeQuery(id+"FgpSSfUhpf4qGKz_2.1.F3.boolean.opBoolean","SPLIT",FACE,{"disambiguationData":[TD([subQ11])],"derivedFrom":makeQuery(id+"FeTh8RoejFn6YHX_2.1.F13.boolean.opBoolean","SPLIT",FACE,{"disambiguationData":[TD([subQ18])],"derivedFrom":makeQuery(id+"FeTh8RoejFn6YHX_2.1.F10.boolean.opBoolean","SPLIT",FACE,{"disambiguationData":[TD([subQ18])],"derivedFrom":makeQuery(id+"FeTh8RoejFn6YHX_2.1.F7.boolean.opBoolean","SPLIT",FACE,{"disambiguationData":[TD([subQ18])],"derivedFrom":makeQuery(id+"F13.boolean.opBoolean","SPLIT",FACE,{"disambiguationData":[TD([subQ24])],"derivedFrom":makeQuery(id+"F10.boolean.opBoolean","SPLIT",FACE,{"disambiguationData":[TD([subQ24])],"derivedFrom":makeQuery(id+"F7.boolean.opBoolean","SPLIT",FACE,{"disambiguationData":[TD([subQ24])],"derivedFrom":makeQuery(id+"F1.opRevolve","SWEPT_FACE",FACE,{"disambiguationData":[OSD([subQ10]),TDD([makeQuery(id+"F0.imprint","IMPRINT",EDGE,{"disambiguationData":[TD([[makeQuery(id+"F0.imprint","INTERSECT",VERTEX,{"derivedFrom":[subQ10,subQ0]}),-1.0]])],"derivedFrom":subQ10})])]})})})})})})})})});}
            var Q29;
            {var subQ0=sQuery(id+"F0.wireOp",EDGE,"E15");var subQ2=sQuery(id+"F0.wireOp",EDGE,"E17");var subQ4=sQuery(id+"F0.wireOp",EDGE,"E9");var subQ5=sQuery(id+"F0.wireOp",EDGE,"E0");var subQ6=makeQuery(id+"FgpSSfUhpf4qGKz_2.1.F3.opRevolve","CAP_FACE",FACE,{"disambiguationData":[OSD([subQ5,subQ4,subQ0,subQ2])],"isStart":true});var subQ12=sQuery(id+"F12.wireOp",EDGE,"E63");var subQ13=sQuery(id+"F12.wireOp",EDGE,"E62");var subQ14=sQuery(id+"F12.wireOp",EDGE,"E61");var subQ15=sQuery(id+"F12.wireOp",EDGE,"E60.1");var subQ16=sQuery(id+"F12.wireOp",EDGE,"E60.0");var subQ18=makeQuery(id+"F13.opRevolve","CAP_FACE",FACE,{"disambiguationData":[OSD([subQ16,subQ15,subQ14,subQ13,subQ12])],"isStart":true});var subQ24=makeQuery(id+"F3.opRevolve","CAP_FACE",FACE,{"disambiguationData":[OSD([subQ5,subQ4,subQ0,subQ2])],"isStart":true});Q29=makeQuery(id+"FgpSSfUhpf4qGKz_2.1.FeTh8RoejFn6YHX_2.1.F7.boolean.opBoolean","SPLIT",FACE,{"disambiguationData":[TD([subQ6])],"derivedFrom":makeQuery(id+"FgpSSfUhpf4qGKz_2.1.F3.boolean.opBoolean","SPLIT",FACE,{"disambiguationData":[TD([subQ6])],"derivedFrom":makeQuery(id+"FeTh8RoejFn6YHX_2.1.F13.boolean.opBoolean","SPLIT",FACE,{"disambiguationData":[TD([subQ18])],"derivedFrom":makeQuery(id+"FeTh8RoejFn6YHX_2.1.F10.boolean.opBoolean","SPLIT",FACE,{"disambiguationData":[TD([subQ18])],"derivedFrom":makeQuery(id+"FeTh8RoejFn6YHX_2.1.F7.boolean.opBoolean","SPLIT",FACE,{"disambiguationData":[TD([subQ18])],"derivedFrom":makeQuery(id+"F13.boolean.opBoolean","SPLIT",FACE,{"disambiguationData":[TD([subQ24])],"derivedFrom":makeQuery(id+"F10.boolean.opBoolean","SPLIT",FACE,{"disambiguationData":[TD([subQ24])],"derivedFrom":makeQuery(id+"F7.boolean.opBoolean","SPLIT",FACE,{"disambiguationData":[TD([subQ24])],"derivedFrom":makeQuery(id+"F1.opRevolve","SWEPT_FACE",FACE,{"disambiguationData":[OSD([subQ5]),TDD([makeQuery(id+"F0.imprint","IMPRINT",EDGE,{"disambiguationData":[TD([[makeQuery(id+"F0.imprint","INTERSECT",VERTEX,{"derivedFrom":[subQ5,subQ0]}),-1.0]])],"derivedFrom":subQ5})])]})})})})})})})})});}
            var Q30;
            {var subQ0=sQuery(id+"F0.wireOp",EDGE,"E15");var subQ2=sQuery(id+"F6.wireOp",EDGE,"E53");var subQ3=sQuery(id+"F6.wireOp",EDGE,"E52");var subQ4=sQuery(id+"F6.wireOp",EDGE,"E51");var subQ5=sQuery(id+"F6.wireOp",EDGE,"E50");var subQ6=sQuery(id+"F6.wireOp",EDGE,"E49.0");var subQ7=makeQuery(id+"FgpSSfUhpf4qGKz_2.1.FeTh8RoejFn6YHX_2.1.F7.opRevolve","CAP_FACE",FACE,{"disambiguationData":[OSD([subQ6,subQ5,subQ4,subQ3,subQ2])],"isStart":false});var subQ8=sQuery(id+"F0.wireOp",EDGE,"E17");var subQ15=sQuery(id+"F12.wireOp",EDGE,"E63");var subQ16=sQuery(id+"F12.wireOp",EDGE,"E62");var subQ17=sQuery(id+"F12.wireOp",EDGE,"E61");var subQ18=sQuery(id+"F12.wireOp",EDGE,"E60.1");var subQ19=sQuery(id+"F12.wireOp",EDGE,"E60.0");var subQ20=makeQuery(id+"FeTh8RoejFn6YHX_2.1.F13.opRevolve","CAP_FACE",FACE,{"disambiguationData":[OSD([subQ19,subQ18,subQ17,subQ16,subQ15])],"isStart":true});var subQ21=sQuery(id+"F0.wireOp",EDGE,"E9");var subQ22=sQuery(id+"F0.wireOp",EDGE,"E0");var subQ23=makeQuery(id+"F13.opRevolve","CAP_FACE",FACE,{"disambiguationData":[OSD([subQ19,subQ18,subQ17,subQ16,subQ15])],"isStart":true});var subQ24=makeQuery(id+"F3.opRevolve","CAP_FACE",FACE,{"disambiguationData":[OSD([subQ22,subQ21,subQ0,subQ8])],"isStart":true});Q30=makeQuery(id+"FgpSSfUhpf4qGKz_2.1.FeTh8RoejFn6YHX_2.1.F10.boolean.opBoolean","SPLIT",FACE,{"disambiguationData":[TD([subQ7])],"derivedFrom":makeQuery(id+"FgpSSfUhpf4qGKz_2.1.FeTh8RoejFn6YHX_2.1.F7.boolean.opBoolean","SPLIT",FACE,{"disambiguationData":[TD([subQ20])],"derivedFrom":makeQuery(id+"FgpSSfUhpf4qGKz_2.1.F3.boolean.opBoolean","SPLIT",FACE,{"disambiguationData":[TD([makeQuery(id+"FgpSSfUhpf4qGKz_2.1.F3.opRevolve","CAP_FACE",FACE,{"disambiguationData":[OSD([subQ22,subQ21,subQ0,subQ8])],"isStart":true})])],"derivedFrom":makeQuery(id+"FeTh8RoejFn6YHX_2.1.F13.boolean.opBoolean","SPLIT",FACE,{"disambiguationData":[TD([subQ23])],"derivedFrom":makeQuery(id+"FeTh8RoejFn6YHX_2.1.F10.boolean.opBoolean","SPLIT",FACE,{"disambiguationData":[TD([subQ23])],"derivedFrom":makeQuery(id+"FeTh8RoejFn6YHX_2.1.F7.boolean.opBoolean","SPLIT",FACE,{"disambiguationData":[TD([subQ23])],"derivedFrom":makeQuery(id+"F13.boolean.opBoolean","SPLIT",FACE,{"disambiguationData":[TD([subQ24])],"derivedFrom":makeQuery(id+"F10.boolean.opBoolean","SPLIT",FACE,{"disambiguationData":[TD([subQ24])],"derivedFrom":makeQuery(id+"F7.boolean.opBoolean","SPLIT",FACE,{"disambiguationData":[TD([subQ24])],"derivedFrom":makeQuery(id+"F1.opRevolve","SWEPT_FACE",FACE,{"disambiguationData":[OSD([subQ22]),TDD([makeQuery(id+"F0.imprint","IMPRINT",EDGE,{"disambiguationData":[TD([[makeQuery(id+"F0.imprint","INTERSECT",VERTEX,{"derivedFrom":[subQ22,subQ0]}),-1.0]])],"derivedFrom":subQ22})])]})})})})})})})})})});}
            var Q31;
            {var subQ0=sQuery(id+"F0.wireOp",EDGE,"E13");var subQ7=sQuery(id+"F0.wireOp",EDGE,"E14");var subQ9=sQuery(id+"F6.wireOp",EDGE,"E53");var subQ10=sQuery(id+"F6.wireOp",EDGE,"E52");var subQ11=sQuery(id+"F6.wireOp",EDGE,"E51");var subQ12=sQuery(id+"F6.wireOp",EDGE,"E50");var subQ13=sQuery(id+"F6.wireOp",EDGE,"E49.0");var subQ14=makeQuery(id+"FgpSSfUhpf4qGKz_2.1.FeTh8RoejFn6YHX_2.1.F7.opRevolve","CAP_FACE",FACE,{"disambiguationData":[OSD([subQ13,subQ12,subQ11,subQ10,subQ9])],"isStart":false});var subQ15=sQuery(id+"F12.wireOp",EDGE,"E63");var subQ16=sQuery(id+"F12.wireOp",EDGE,"E62");var subQ17=sQuery(id+"F12.wireOp",EDGE,"E61");var subQ18=sQuery(id+"F12.wireOp",EDGE,"E60.1");var subQ19=sQuery(id+"F12.wireOp",EDGE,"E60.0");var subQ20=makeQuery(id+"FeTh8RoejFn6YHX_2.1.F13.opRevolve","CAP_FACE",FACE,{"disambiguationData":[OSD([subQ19,subQ18,subQ17,subQ16,subQ15])],"isStart":true});var subQ21=sQuery(id+"F0.wireOp",EDGE,"E9");var subQ22=sQuery(id+"F0.wireOp",EDGE,"E0");var subQ23=makeQuery(id+"F13.opRevolve","CAP_FACE",FACE,{"disambiguationData":[OSD([subQ19,subQ18,subQ17,subQ16,subQ15])],"isStart":true});var subQ24=makeQuery(id+"F3.opRevolve","CAP_FACE",FACE,{"disambiguationData":[OSD([subQ22,subQ21,subQ0,subQ7])],"isStart":true});Q31=makeQuery(id+"FgpSSfUhpf4qGKz_2.1.FeTh8RoejFn6YHX_2.1.F10.boolean.opBoolean","SPLIT",FACE,{"disambiguationData":[TD([subQ14])],"derivedFrom":makeQuery(id+"FgpSSfUhpf4qGKz_2.1.FeTh8RoejFn6YHX_2.1.F7.boolean.opBoolean","SPLIT",FACE,{"disambiguationData":[TD([subQ20])],"derivedFrom":makeQuery(id+"FgpSSfUhpf4qGKz_2.1.F3.boolean.opBoolean","SPLIT",FACE,{"disambiguationData":[TD([makeQuery(id+"FgpSSfUhpf4qGKz_2.1.F3.opRevolve","CAP_FACE",FACE,{"disambiguationData":[OSD([subQ22,subQ21,subQ0,subQ7])],"isStart":true})])],"derivedFrom":makeQuery(id+"FeTh8RoejFn6YHX_2.1.F13.boolean.opBoolean","SPLIT",FACE,{"disambiguationData":[TD([subQ23])],"derivedFrom":makeQuery(id+"FeTh8RoejFn6YHX_2.1.F10.boolean.opBoolean","SPLIT",FACE,{"disambiguationData":[TD([subQ23])],"derivedFrom":makeQuery(id+"FeTh8RoejFn6YHX_2.1.F7.boolean.opBoolean","SPLIT",FACE,{"disambiguationData":[TD([subQ23])],"derivedFrom":makeQuery(id+"F13.boolean.opBoolean","SPLIT",FACE,{"disambiguationData":[TD([subQ24])],"derivedFrom":makeQuery(id+"F10.boolean.opBoolean","SPLIT",FACE,{"disambiguationData":[TD([subQ24])],"derivedFrom":makeQuery(id+"F7.boolean.opBoolean","SPLIT",FACE,{"disambiguationData":[TD([subQ24])],"derivedFrom":makeQuery(id+"F1.opRevolve","SWEPT_FACE",FACE,{"disambiguationData":[OSD([subQ22]),TDD([makeQuery(id+"F0.imprint","IMPRINT",EDGE,{"disambiguationData":[TD([[makeQuery(id+"F0.imprint","INTERSECT",VERTEX,{"derivedFrom":[subQ22,subQ0]}),-1.0]])],"derivedFrom":subQ22})])]})})})})})})})})})});}
            var Q32;
            {var subQ0=sQuery(id+"F0.wireOp",EDGE,"E13");var subQ2=sQuery(id+"F0.wireOp",EDGE,"E14");var subQ4=sQuery(id+"F9.wireOp",EDGE,"E59");var subQ5=sQuery(id+"F9.wireOp",EDGE,"E58");var subQ6=sQuery(id+"F9.wireOp",EDGE,"E57");var subQ7=sQuery(id+"F9.wireOp",EDGE,"E56");var subQ8=sQuery(id+"F9.wireOp",EDGE,"E55");var subQ9=makeQuery(id+"FgpSSfUhpf4qGKz_2.1.FeTh8RoejFn6YHX_2.1.F10.opRevolve","CAP_FACE",FACE,{"disambiguationData":[OSD([subQ8,subQ7,subQ6,subQ5,subQ4])],"isStart":true});var subQ10=sQuery(id+"F12.wireOp",EDGE,"E63");var subQ11=sQuery(id+"F12.wireOp",EDGE,"E62");var subQ12=sQuery(id+"F12.wireOp",EDGE,"E61");var subQ13=sQuery(id+"F12.wireOp",EDGE,"E60.1");var subQ14=sQuery(id+"F12.wireOp",EDGE,"E60.0");var subQ15=makeQuery(id+"FeTh8RoejFn6YHX_2.1.F13.opRevolve","CAP_FACE",FACE,{"disambiguationData":[OSD([subQ14,subQ13,subQ12,subQ11,subQ10])],"isStart":true});var subQ21=sQuery(id+"F0.wireOp",EDGE,"E9");var subQ22=sQuery(id+"F0.wireOp",EDGE,"E0");var subQ23=makeQuery(id+"F13.opRevolve","CAP_FACE",FACE,{"disambiguationData":[OSD([subQ14,subQ13,subQ12,subQ11,subQ10])],"isStart":true});var subQ24=makeQuery(id+"F3.opRevolve","CAP_FACE",FACE,{"disambiguationData":[OSD([subQ22,subQ21,subQ0,subQ2])],"isStart":true});Q32=makeQuery(id+"FgpSSfUhpf4qGKz_2.1.FeTh8RoejFn6YHX_2.1.F13.boolean.opBoolean","SPLIT",FACE,{"disambiguationData":[TD([subQ9])],"derivedFrom":makeQuery(id+"FgpSSfUhpf4qGKz_2.1.FeTh8RoejFn6YHX_2.1.F10.boolean.opBoolean","SPLIT",FACE,{"disambiguationData":[TD([subQ15])],"derivedFrom":makeQuery(id+"FgpSSfUhpf4qGKz_2.1.FeTh8RoejFn6YHX_2.1.F7.boolean.opBoolean","SPLIT",FACE,{"disambiguationData":[TD([subQ15])],"derivedFrom":makeQuery(id+"FgpSSfUhpf4qGKz_2.1.F3.boolean.opBoolean","SPLIT",FACE,{"disambiguationData":[TD([makeQuery(id+"FgpSSfUhpf4qGKz_2.1.F3.opRevolve","CAP_FACE",FACE,{"disambiguationData":[OSD([subQ22,subQ21,subQ0,subQ2])],"isStart":true})])],"derivedFrom":makeQuery(id+"FeTh8RoejFn6YHX_2.1.F13.boolean.opBoolean","SPLIT",FACE,{"disambiguationData":[TD([subQ23])],"derivedFrom":makeQuery(id+"FeTh8RoejFn6YHX_2.1.F10.boolean.opBoolean","SPLIT",FACE,{"disambiguationData":[TD([subQ23])],"derivedFrom":makeQuery(id+"FeTh8RoejFn6YHX_2.1.F7.boolean.opBoolean","SPLIT",FACE,{"disambiguationData":[TD([subQ23])],"derivedFrom":makeQuery(id+"F13.boolean.opBoolean","SPLIT",FACE,{"disambiguationData":[TD([subQ24])],"derivedFrom":makeQuery(id+"F10.boolean.opBoolean","SPLIT",FACE,{"disambiguationData":[TD([subQ24])],"derivedFrom":makeQuery(id+"F7.boolean.opBoolean","SPLIT",FACE,{"disambiguationData":[TD([subQ24])],"derivedFrom":makeQuery(id+"F1.opRevolve","SWEPT_FACE",FACE,{"disambiguationData":[OSD([subQ22]),TDD([makeQuery(id+"F0.imprint","IMPRINT",EDGE,{"disambiguationData":[TD([[makeQuery(id+"F0.imprint","INTERSECT",VERTEX,{"derivedFrom":[subQ22,subQ0]}),-1.0]])],"derivedFrom":subQ22})])]})})})})})})})})})})});}
            var Q33;
            {var subQ0=sQuery(id+"F0.wireOp",EDGE,"E15");var subQ2=sQuery(id+"F0.wireOp",EDGE,"E17");var subQ4=sQuery(id+"F12.wireOp",EDGE,"E63");var subQ5=sQuery(id+"F12.wireOp",EDGE,"E62");var subQ6=sQuery(id+"F12.wireOp",EDGE,"E61");var subQ7=sQuery(id+"F12.wireOp",EDGE,"E60.1");var subQ8=sQuery(id+"F12.wireOp",EDGE,"E60.0");var subQ9=sQuery(id+"F9.wireOp",EDGE,"E59");var subQ10=sQuery(id+"F9.wireOp",EDGE,"E58");var subQ11=sQuery(id+"F9.wireOp",EDGE,"E57");var subQ12=sQuery(id+"F9.wireOp",EDGE,"E56");var subQ13=sQuery(id+"F9.wireOp",EDGE,"E55");var subQ14=makeQuery(id+"FgpSSfUhpf4qGKz_2.1.FeTh8RoejFn6YHX_2.1.F10.opRevolve","CAP_FACE",FACE,{"disambiguationData":[OSD([subQ13,subQ12,subQ11,subQ10,subQ9])],"isStart":true});var subQ15=makeQuery(id+"FeTh8RoejFn6YHX_2.1.F13.opRevolve","CAP_FACE",FACE,{"disambiguationData":[OSD([subQ8,subQ7,subQ6,subQ5,subQ4])],"isStart":true});var subQ21=sQuery(id+"F0.wireOp",EDGE,"E9");var subQ22=sQuery(id+"F0.wireOp",EDGE,"E0");var subQ23=makeQuery(id+"F13.opRevolve","CAP_FACE",FACE,{"disambiguationData":[OSD([subQ8,subQ7,subQ6,subQ5,subQ4])],"isStart":true});var subQ24=makeQuery(id+"F3.opRevolve","CAP_FACE",FACE,{"disambiguationData":[OSD([subQ22,subQ21,subQ0,subQ2])],"isStart":true});Q33=makeQuery(id+"FgpSSfUhpf4qGKz_2.1.FeTh8RoejFn6YHX_2.1.F13.boolean.opBoolean","SPLIT",FACE,{"disambiguationData":[TD([subQ14])],"derivedFrom":makeQuery(id+"FgpSSfUhpf4qGKz_2.1.FeTh8RoejFn6YHX_2.1.F10.boolean.opBoolean","SPLIT",FACE,{"disambiguationData":[TD([subQ15])],"derivedFrom":makeQuery(id+"FgpSSfUhpf4qGKz_2.1.FeTh8RoejFn6YHX_2.1.F7.boolean.opBoolean","SPLIT",FACE,{"disambiguationData":[TD([subQ15])],"derivedFrom":makeQuery(id+"FgpSSfUhpf4qGKz_2.1.F3.boolean.opBoolean","SPLIT",FACE,{"disambiguationData":[TD([makeQuery(id+"FgpSSfUhpf4qGKz_2.1.F3.opRevolve","CAP_FACE",FACE,{"disambiguationData":[OSD([subQ22,subQ21,subQ0,subQ2])],"isStart":true})])],"derivedFrom":makeQuery(id+"FeTh8RoejFn6YHX_2.1.F13.boolean.opBoolean","SPLIT",FACE,{"disambiguationData":[TD([subQ23])],"derivedFrom":makeQuery(id+"FeTh8RoejFn6YHX_2.1.F10.boolean.opBoolean","SPLIT",FACE,{"disambiguationData":[TD([subQ23])],"derivedFrom":makeQuery(id+"FeTh8RoejFn6YHX_2.1.F7.boolean.opBoolean","SPLIT",FACE,{"disambiguationData":[TD([subQ23])],"derivedFrom":makeQuery(id+"F13.boolean.opBoolean","SPLIT",FACE,{"disambiguationData":[TD([subQ24])],"derivedFrom":makeQuery(id+"F10.boolean.opBoolean","SPLIT",FACE,{"disambiguationData":[TD([subQ24])],"derivedFrom":makeQuery(id+"F7.boolean.opBoolean","SPLIT",FACE,{"disambiguationData":[TD([subQ24])],"derivedFrom":makeQuery(id+"F1.opRevolve","SWEPT_FACE",FACE,{"disambiguationData":[OSD([subQ22]),TDD([makeQuery(id+"F0.imprint","IMPRINT",EDGE,{"disambiguationData":[TD([[makeQuery(id+"F0.imprint","INTERSECT",VERTEX,{"derivedFrom":[subQ22,subQ0]}),-1.0]])],"derivedFrom":subQ22})])]})})})})})})})})})})});}
            var Q34;
            {var subQ0=sQuery(id+"F0.wireOp",EDGE,"E15");var subQ2=sQuery(id+"F12.wireOp",EDGE,"E63");var subQ3=sQuery(id+"F12.wireOp",EDGE,"E62");var subQ4=sQuery(id+"F12.wireOp",EDGE,"E61");var subQ5=sQuery(id+"F12.wireOp",EDGE,"E60.1");var subQ6=sQuery(id+"F12.wireOp",EDGE,"E60.0");var subQ7=sQuery(id+"F0.wireOp",EDGE,"E17");var subQ9=sQuery(id+"F9.wireOp",EDGE,"E59");var subQ10=sQuery(id+"F9.wireOp",EDGE,"E58");var subQ11=sQuery(id+"F9.wireOp",EDGE,"E57");var subQ12=sQuery(id+"F9.wireOp",EDGE,"E56");var subQ13=sQuery(id+"F9.wireOp",EDGE,"E55");var subQ14=makeQuery(id+"FeTh8RoejFn6YHX_2.1.F10.opRevolve","CAP_FACE",FACE,{"disambiguationData":[OSD([subQ13,subQ12,subQ11,subQ10,subQ9])],"isStart":true});var subQ15=makeQuery(id+"F13.opRevolve","CAP_FACE",FACE,{"disambiguationData":[OSD([subQ6,subQ5,subQ4,subQ3,subQ2])],"isStart":true});var subQ21=sQuery(id+"F0.wireOp",EDGE,"E0");var subQ22=makeQuery(id+"F3.opRevolve","CAP_FACE",FACE,{"disambiguationData":[OSD([subQ21,sQuery(id+"F0.wireOp",EDGE,"E9"),subQ0,subQ7])],"isStart":true});Q34=makeQuery(id+"FeTh8RoejFn6YHX_2.1.F13.boolean.opBoolean","SPLIT",FACE,{"disambiguationData":[TD([subQ14])],"derivedFrom":makeQuery(id+"FeTh8RoejFn6YHX_2.1.F10.boolean.opBoolean","SPLIT",FACE,{"disambiguationData":[TD([subQ15])],"derivedFrom":makeQuery(id+"FeTh8RoejFn6YHX_2.1.F7.boolean.opBoolean","SPLIT",FACE,{"disambiguationData":[TD([subQ15])],"derivedFrom":makeQuery(id+"F13.boolean.opBoolean","SPLIT",FACE,{"disambiguationData":[TD([subQ22])],"derivedFrom":makeQuery(id+"F10.boolean.opBoolean","SPLIT",FACE,{"disambiguationData":[TD([subQ22])],"derivedFrom":makeQuery(id+"F7.boolean.opBoolean","SPLIT",FACE,{"disambiguationData":[TD([subQ22])],"derivedFrom":makeQuery(id+"F1.opRevolve","SWEPT_FACE",FACE,{"disambiguationData":[OSD([subQ21]),TDD([makeQuery(id+"F0.imprint","IMPRINT",EDGE,{"disambiguationData":[TD([[makeQuery(id+"F0.imprint","INTERSECT",VERTEX,{"derivedFrom":[subQ21,subQ0]}),-1.0]])],"derivedFrom":subQ21})])]})})})})})})});}
            var Q35;
            {var subQ0=sQuery(id+"F0.wireOp",EDGE,"E15");var subQ2=sQuery(id+"F12.wireOp",EDGE,"E63");var subQ3=sQuery(id+"F12.wireOp",EDGE,"E62");var subQ4=sQuery(id+"F12.wireOp",EDGE,"E61");var subQ5=sQuery(id+"F12.wireOp",EDGE,"E60.1");var subQ6=sQuery(id+"F12.wireOp",EDGE,"E60.0");var subQ7=sQuery(id+"F0.wireOp",EDGE,"E17");var subQ9=makeQuery(id+"FeTh8RoejFn6YHX_2.1.F13.opRevolve","CAP_FACE",FACE,{"disambiguationData":[OSD([subQ6,subQ5,subQ4,subQ3,subQ2])],"isStart":true});var subQ20=sQuery(id+"F0.wireOp",EDGE,"E9");var subQ21=sQuery(id+"F0.wireOp",EDGE,"E0");var subQ22=makeQuery(id+"F13.opRevolve","CAP_FACE",FACE,{"disambiguationData":[OSD([subQ6,subQ5,subQ4,subQ3,subQ2])],"isStart":true});var subQ23=makeQuery(id+"F3.opRevolve","CAP_FACE",FACE,{"disambiguationData":[OSD([subQ21,subQ20,subQ0,subQ7])],"isStart":true});Q35=makeQuery(id+"FgpSSfUhpf4qGKz_2.1.FeTh8RoejFn6YHX_2.1.F13.boolean.opBoolean","SPLIT",FACE,{"disambiguationData":[TD([subQ9])],"derivedFrom":makeQuery(id+"FgpSSfUhpf4qGKz_2.1.FeTh8RoejFn6YHX_2.1.F10.boolean.opBoolean","SPLIT",FACE,{"disambiguationData":[TD([subQ9])],"derivedFrom":makeQuery(id+"FgpSSfUhpf4qGKz_2.1.FeTh8RoejFn6YHX_2.1.F7.boolean.opBoolean","SPLIT",FACE,{"disambiguationData":[TD([subQ9])],"derivedFrom":makeQuery(id+"FgpSSfUhpf4qGKz_2.1.F3.boolean.opBoolean","SPLIT",FACE,{"disambiguationData":[TD([makeQuery(id+"FgpSSfUhpf4qGKz_2.1.F3.opRevolve","CAP_FACE",FACE,{"disambiguationData":[OSD([subQ21,subQ20,subQ0,subQ7])],"isStart":true})])],"derivedFrom":makeQuery(id+"FeTh8RoejFn6YHX_2.1.F13.boolean.opBoolean","SPLIT",FACE,{"disambiguationData":[TD([subQ22])],"derivedFrom":makeQuery(id+"FeTh8RoejFn6YHX_2.1.F10.boolean.opBoolean","SPLIT",FACE,{"disambiguationData":[TD([subQ22])],"derivedFrom":makeQuery(id+"FeTh8RoejFn6YHX_2.1.F7.boolean.opBoolean","SPLIT",FACE,{"disambiguationData":[TD([subQ22])],"derivedFrom":makeQuery(id+"F13.boolean.opBoolean","SPLIT",FACE,{"disambiguationData":[TD([subQ23])],"derivedFrom":makeQuery(id+"F10.boolean.opBoolean","SPLIT",FACE,{"disambiguationData":[TD([subQ23])],"derivedFrom":makeQuery(id+"F7.boolean.opBoolean","SPLIT",FACE,{"disambiguationData":[TD([subQ23])],"derivedFrom":makeQuery(id+"F1.opRevolve","SWEPT_FACE",FACE,{"disambiguationData":[OSD([subQ21]),TDD([makeQuery(id+"F0.imprint","IMPRINT",EDGE,{"disambiguationData":[TD([[makeQuery(id+"F0.imprint","INTERSECT",VERTEX,{"derivedFrom":[subQ21,subQ0]}),-1.0]])],"derivedFrom":subQ21})])]})})})})})})})})})})});}
            var Q36;
            {var subQ0=sQuery(id+"F0.wireOp",EDGE,"E13");var subQ2=sQuery(id+"F0.wireOp",EDGE,"E14");var subQ4=sQuery(id+"F12.wireOp",EDGE,"E63");var subQ5=sQuery(id+"F12.wireOp",EDGE,"E62");var subQ6=sQuery(id+"F12.wireOp",EDGE,"E61");var subQ7=sQuery(id+"F12.wireOp",EDGE,"E60.1");var subQ8=sQuery(id+"F12.wireOp",EDGE,"E60.0");var subQ9=makeQuery(id+"FeTh8RoejFn6YHX_2.1.F13.opRevolve","CAP_FACE",FACE,{"disambiguationData":[OSD([subQ8,subQ7,subQ6,subQ5,subQ4])],"isStart":true});var subQ20=sQuery(id+"F0.wireOp",EDGE,"E9");var subQ21=sQuery(id+"F0.wireOp",EDGE,"E0");var subQ22=makeQuery(id+"F13.opRevolve","CAP_FACE",FACE,{"disambiguationData":[OSD([subQ8,subQ7,subQ6,subQ5,subQ4])],"isStart":true});var subQ23=makeQuery(id+"F3.opRevolve","CAP_FACE",FACE,{"disambiguationData":[OSD([subQ21,subQ20,subQ0,subQ2])],"isStart":true});Q36=makeQuery(id+"FgpSSfUhpf4qGKz_2.1.FeTh8RoejFn6YHX_2.1.F13.boolean.opBoolean","SPLIT",FACE,{"disambiguationData":[TD([subQ9])],"derivedFrom":makeQuery(id+"FgpSSfUhpf4qGKz_2.1.FeTh8RoejFn6YHX_2.1.F10.boolean.opBoolean","SPLIT",FACE,{"disambiguationData":[TD([subQ9])],"derivedFrom":makeQuery(id+"FgpSSfUhpf4qGKz_2.1.FeTh8RoejFn6YHX_2.1.F7.boolean.opBoolean","SPLIT",FACE,{"disambiguationData":[TD([subQ9])],"derivedFrom":makeQuery(id+"FgpSSfUhpf4qGKz_2.1.F3.boolean.opBoolean","SPLIT",FACE,{"disambiguationData":[TD([makeQuery(id+"FgpSSfUhpf4qGKz_2.1.F3.opRevolve","CAP_FACE",FACE,{"disambiguationData":[OSD([subQ21,subQ20,subQ0,subQ2])],"isStart":true})])],"derivedFrom":makeQuery(id+"FeTh8RoejFn6YHX_2.1.F13.boolean.opBoolean","SPLIT",FACE,{"disambiguationData":[TD([subQ22])],"derivedFrom":makeQuery(id+"FeTh8RoejFn6YHX_2.1.F10.boolean.opBoolean","SPLIT",FACE,{"disambiguationData":[TD([subQ22])],"derivedFrom":makeQuery(id+"FeTh8RoejFn6YHX_2.1.F7.boolean.opBoolean","SPLIT",FACE,{"disambiguationData":[TD([subQ22])],"derivedFrom":makeQuery(id+"F13.boolean.opBoolean","SPLIT",FACE,{"disambiguationData":[TD([subQ23])],"derivedFrom":makeQuery(id+"F10.boolean.opBoolean","SPLIT",FACE,{"disambiguationData":[TD([subQ23])],"derivedFrom":makeQuery(id+"F7.boolean.opBoolean","SPLIT",FACE,{"disambiguationData":[TD([subQ23])],"derivedFrom":makeQuery(id+"F1.opRevolve","SWEPT_FACE",FACE,{"disambiguationData":[OSD([subQ21]),TDD([makeQuery(id+"F0.imprint","IMPRINT",EDGE,{"disambiguationData":[TD([[makeQuery(id+"F0.imprint","INTERSECT",VERTEX,{"derivedFrom":[subQ21,subQ0]}),-1.0]])],"derivedFrom":subQ21})])]})})})})})})})})})})});}
            var Q37;
            {var subQ0=sQuery(id+"F0.wireOp",EDGE,"E13");var subQ2=sQuery(id+"F0.wireOp",EDGE,"E14");var subQ4=sQuery(id+"F9.wireOp",EDGE,"E59");var subQ5=sQuery(id+"F9.wireOp",EDGE,"E58");var subQ6=sQuery(id+"F9.wireOp",EDGE,"E57");var subQ7=sQuery(id+"F9.wireOp",EDGE,"E56");var subQ8=sQuery(id+"F9.wireOp",EDGE,"E55");var subQ9=makeQuery(id+"FeTh8RoejFn6YHX_2.1.F10.opRevolve","CAP_FACE",FACE,{"disambiguationData":[OSD([subQ8,subQ7,subQ6,subQ5,subQ4])],"isStart":true});var subQ10=sQuery(id+"F12.wireOp",EDGE,"E63");var subQ11=sQuery(id+"F12.wireOp",EDGE,"E62");var subQ12=sQuery(id+"F12.wireOp",EDGE,"E61");var subQ13=sQuery(id+"F12.wireOp",EDGE,"E60.1");var subQ14=sQuery(id+"F12.wireOp",EDGE,"E60.0");var subQ15=makeQuery(id+"F13.opRevolve","CAP_FACE",FACE,{"disambiguationData":[OSD([subQ14,subQ13,subQ12,subQ11,subQ10])],"isStart":true});var subQ21=sQuery(id+"F0.wireOp",EDGE,"E0");var subQ22=makeQuery(id+"F3.opRevolve","CAP_FACE",FACE,{"disambiguationData":[OSD([subQ21,sQuery(id+"F0.wireOp",EDGE,"E9"),subQ0,subQ2])],"isStart":true});Q37=makeQuery(id+"FeTh8RoejFn6YHX_2.1.F13.boolean.opBoolean","SPLIT",FACE,{"disambiguationData":[TD([subQ9])],"derivedFrom":makeQuery(id+"FeTh8RoejFn6YHX_2.1.F10.boolean.opBoolean","SPLIT",FACE,{"disambiguationData":[TD([subQ15])],"derivedFrom":makeQuery(id+"FeTh8RoejFn6YHX_2.1.F7.boolean.opBoolean","SPLIT",FACE,{"disambiguationData":[TD([subQ15])],"derivedFrom":makeQuery(id+"F13.boolean.opBoolean","SPLIT",FACE,{"disambiguationData":[TD([subQ22])],"derivedFrom":makeQuery(id+"F10.boolean.opBoolean","SPLIT",FACE,{"disambiguationData":[TD([subQ22])],"derivedFrom":makeQuery(id+"F7.boolean.opBoolean","SPLIT",FACE,{"disambiguationData":[TD([subQ22])],"derivedFrom":makeQuery(id+"F1.opRevolve","SWEPT_FACE",FACE,{"disambiguationData":[OSD([subQ21]),TDD([makeQuery(id+"F0.imprint","IMPRINT",EDGE,{"disambiguationData":[TD([[makeQuery(id+"F0.imprint","INTERSECT",VERTEX,{"derivedFrom":[subQ21,subQ0]}),-1.0]])],"derivedFrom":subQ21})])]})})})})})})});}
            var Q38;
            {var subQ0=sQuery(id+"F0.wireOp",EDGE,"E15");var subQ2=sQuery(id+"F0.wireOp",EDGE,"E17");var subQ4=sQuery(id+"F6.wireOp",EDGE,"E53");var subQ5=sQuery(id+"F6.wireOp",EDGE,"E52");var subQ6=sQuery(id+"F6.wireOp",EDGE,"E51");var subQ7=sQuery(id+"F6.wireOp",EDGE,"E50");var subQ8=sQuery(id+"F6.wireOp",EDGE,"E49.0");var subQ9=makeQuery(id+"FeTh8RoejFn6YHX_2.1.F7.opRevolve","CAP_FACE",FACE,{"disambiguationData":[OSD([subQ8,subQ7,subQ6,subQ5,subQ4])],"isStart":false});var subQ15=makeQuery(id+"F13.opRevolve","CAP_FACE",FACE,{"disambiguationData":[OSD([sQuery(id+"F12.wireOp",EDGE,"E60.0"),sQuery(id+"F12.wireOp",EDGE,"E60.1"),sQuery(id+"F12.wireOp",EDGE,"E61"),sQuery(id+"F12.wireOp",EDGE,"E62"),sQuery(id+"F12.wireOp",EDGE,"E63")])],"isStart":true});var subQ16=sQuery(id+"F0.wireOp",EDGE,"E0");var subQ17=makeQuery(id+"F3.opRevolve","CAP_FACE",FACE,{"disambiguationData":[OSD([subQ16,sQuery(id+"F0.wireOp",EDGE,"E9"),subQ0,subQ2])],"isStart":true});Q38=makeQuery(id+"FeTh8RoejFn6YHX_2.1.F10.boolean.opBoolean","SPLIT",FACE,{"disambiguationData":[TD([subQ9])],"derivedFrom":makeQuery(id+"FeTh8RoejFn6YHX_2.1.F7.boolean.opBoolean","SPLIT",FACE,{"disambiguationData":[TD([subQ15])],"derivedFrom":makeQuery(id+"F13.boolean.opBoolean","SPLIT",FACE,{"disambiguationData":[TD([subQ17])],"derivedFrom":makeQuery(id+"F10.boolean.opBoolean","SPLIT",FACE,{"disambiguationData":[TD([subQ17])],"derivedFrom":makeQuery(id+"F7.boolean.opBoolean","SPLIT",FACE,{"disambiguationData":[TD([subQ17])],"derivedFrom":makeQuery(id+"F1.opRevolve","SWEPT_FACE",FACE,{"disambiguationData":[OSD([subQ16]),TDD([makeQuery(id+"F0.imprint","IMPRINT",EDGE,{"disambiguationData":[TD([[makeQuery(id+"F0.imprint","INTERSECT",VERTEX,{"derivedFrom":[subQ16,subQ0]}),-1.0]])],"derivedFrom":subQ16})])]})})})})})});}
            var Q39;
            {var subQ0=sQuery(id+"F0.wireOp",EDGE,"E15");var subQ2=sQuery(id+"F0.wireOp",EDGE,"E17");var subQ3=sQuery(id+"F0.wireOp",EDGE,"E0");var subQ4=makeQuery(id+"F3.opRevolve","CAP_FACE",FACE,{"disambiguationData":[OSD([subQ3,sQuery(id+"F0.wireOp",EDGE,"E9"),subQ0,subQ2])],"isStart":true});Q39=makeQuery(id+"FeTh8RoejFn6YHX_2.1.F7.boolean.opBoolean","SPLIT",FACE,{"disambiguationData":[TD([subQ4])],"derivedFrom":makeQuery(id+"F13.boolean.opBoolean","SPLIT",FACE,{"disambiguationData":[TD([subQ4])],"derivedFrom":makeQuery(id+"F10.boolean.opBoolean","SPLIT",FACE,{"disambiguationData":[TD([subQ4])],"derivedFrom":makeQuery(id+"F7.boolean.opBoolean","SPLIT",FACE,{"disambiguationData":[TD([subQ4])],"derivedFrom":makeQuery(id+"F1.opRevolve","SWEPT_FACE",FACE,{"disambiguationData":[OSD([subQ3]),TDD([makeQuery(id+"F0.imprint","IMPRINT",EDGE,{"disambiguationData":[TD([[makeQuery(id+"F0.imprint","INTERSECT",VERTEX,{"derivedFrom":[subQ3,subQ0]}),-1.0]])],"derivedFrom":subQ3})])]})})})})});}
            var Q40;
            {var subQ0=sQuery(id+"F0.wireOp",EDGE,"E13");var subQ7=sQuery(id+"F0.wireOp",EDGE,"E14");var subQ9=sQuery(id+"F0.wireOp",EDGE,"E0");var subQ10=makeQuery(id+"F3.opRevolve","CAP_FACE",FACE,{"disambiguationData":[OSD([subQ9,sQuery(id+"F0.wireOp",EDGE,"E9"),subQ0,subQ7])],"isStart":true});Q40=makeQuery(id+"FeTh8RoejFn6YHX_2.1.F7.boolean.opBoolean","SPLIT",FACE,{"disambiguationData":[TD([subQ10])],"derivedFrom":makeQuery(id+"F13.boolean.opBoolean","SPLIT",FACE,{"disambiguationData":[TD([subQ10])],"derivedFrom":makeQuery(id+"F10.boolean.opBoolean","SPLIT",FACE,{"disambiguationData":[TD([subQ10])],"derivedFrom":makeQuery(id+"F7.boolean.opBoolean","SPLIT",FACE,{"disambiguationData":[TD([subQ10])],"derivedFrom":makeQuery(id+"F1.opRevolve","SWEPT_FACE",FACE,{"disambiguationData":[OSD([subQ9]),TDD([makeQuery(id+"F0.imprint","IMPRINT",EDGE,{"disambiguationData":[TD([[makeQuery(id+"F0.imprint","INTERSECT",VERTEX,{"derivedFrom":[subQ9,subQ0]}),-1.0]])],"derivedFrom":subQ9})])]})})})})});}
            var Q41;
            {var subQ0=sQuery(id+"F0.wireOp",EDGE,"E13");var subQ2=sQuery(id+"F0.wireOp",EDGE,"E14");var subQ4=sQuery(id+"F6.wireOp",EDGE,"E53");var subQ5=sQuery(id+"F6.wireOp",EDGE,"E52");var subQ6=sQuery(id+"F6.wireOp",EDGE,"E51");var subQ7=sQuery(id+"F6.wireOp",EDGE,"E50");var subQ8=sQuery(id+"F6.wireOp",EDGE,"E49.0");var subQ9=makeQuery(id+"FeTh8RoejFn6YHX_2.1.F7.opRevolve","CAP_FACE",FACE,{"disambiguationData":[OSD([subQ8,subQ7,subQ6,subQ5,subQ4])],"isStart":false});var subQ15=makeQuery(id+"F13.opRevolve","CAP_FACE",FACE,{"disambiguationData":[OSD([sQuery(id+"F12.wireOp",EDGE,"E60.0"),sQuery(id+"F12.wireOp",EDGE,"E60.1"),sQuery(id+"F12.wireOp",EDGE,"E61"),sQuery(id+"F12.wireOp",EDGE,"E62"),sQuery(id+"F12.wireOp",EDGE,"E63")])],"isStart":true});var subQ16=sQuery(id+"F0.wireOp",EDGE,"E0");var subQ17=makeQuery(id+"F3.opRevolve","CAP_FACE",FACE,{"disambiguationData":[OSD([subQ16,sQuery(id+"F0.wireOp",EDGE,"E9"),subQ0,subQ2])],"isStart":true});Q41=makeQuery(id+"FeTh8RoejFn6YHX_2.1.F10.boolean.opBoolean","SPLIT",FACE,{"disambiguationData":[TD([subQ9])],"derivedFrom":makeQuery(id+"FeTh8RoejFn6YHX_2.1.F7.boolean.opBoolean","SPLIT",FACE,{"disambiguationData":[TD([subQ15])],"derivedFrom":makeQuery(id+"F13.boolean.opBoolean","SPLIT",FACE,{"disambiguationData":[TD([subQ17])],"derivedFrom":makeQuery(id+"F10.boolean.opBoolean","SPLIT",FACE,{"disambiguationData":[TD([subQ17])],"derivedFrom":makeQuery(id+"F7.boolean.opBoolean","SPLIT",FACE,{"disambiguationData":[TD([subQ17])],"derivedFrom":makeQuery(id+"F1.opRevolve","SWEPT_FACE",FACE,{"disambiguationData":[OSD([subQ16]),TDD([makeQuery(id+"F0.imprint","IMPRINT",EDGE,{"disambiguationData":[TD([[makeQuery(id+"F0.imprint","INTERSECT",VERTEX,{"derivedFrom":[subQ16,subQ0]}),-1.0]])],"derivedFrom":subQ16})])]})})})})})});}
            chamfer(context, id + "F14", {"entities" : qUnion([Q0, Q1, Q2, Q3, Q4, Q5, Q6, Q7, Q8, Q9, Q10, Q11, Q12, Q13, Q14, Q15, Q16, Q17, Q18, Q19, Q20, Q21, Q22, Q23, Q24, Q25, Q26, Q27, Q28, Q29, Q30, Q31, Q32, Q33, Q34, Q35, Q36, Q37, Q38, Q39, Q40, Q41]), "width" : 0.64 * mm, "tangentPropagation" : true});
        }
    });
